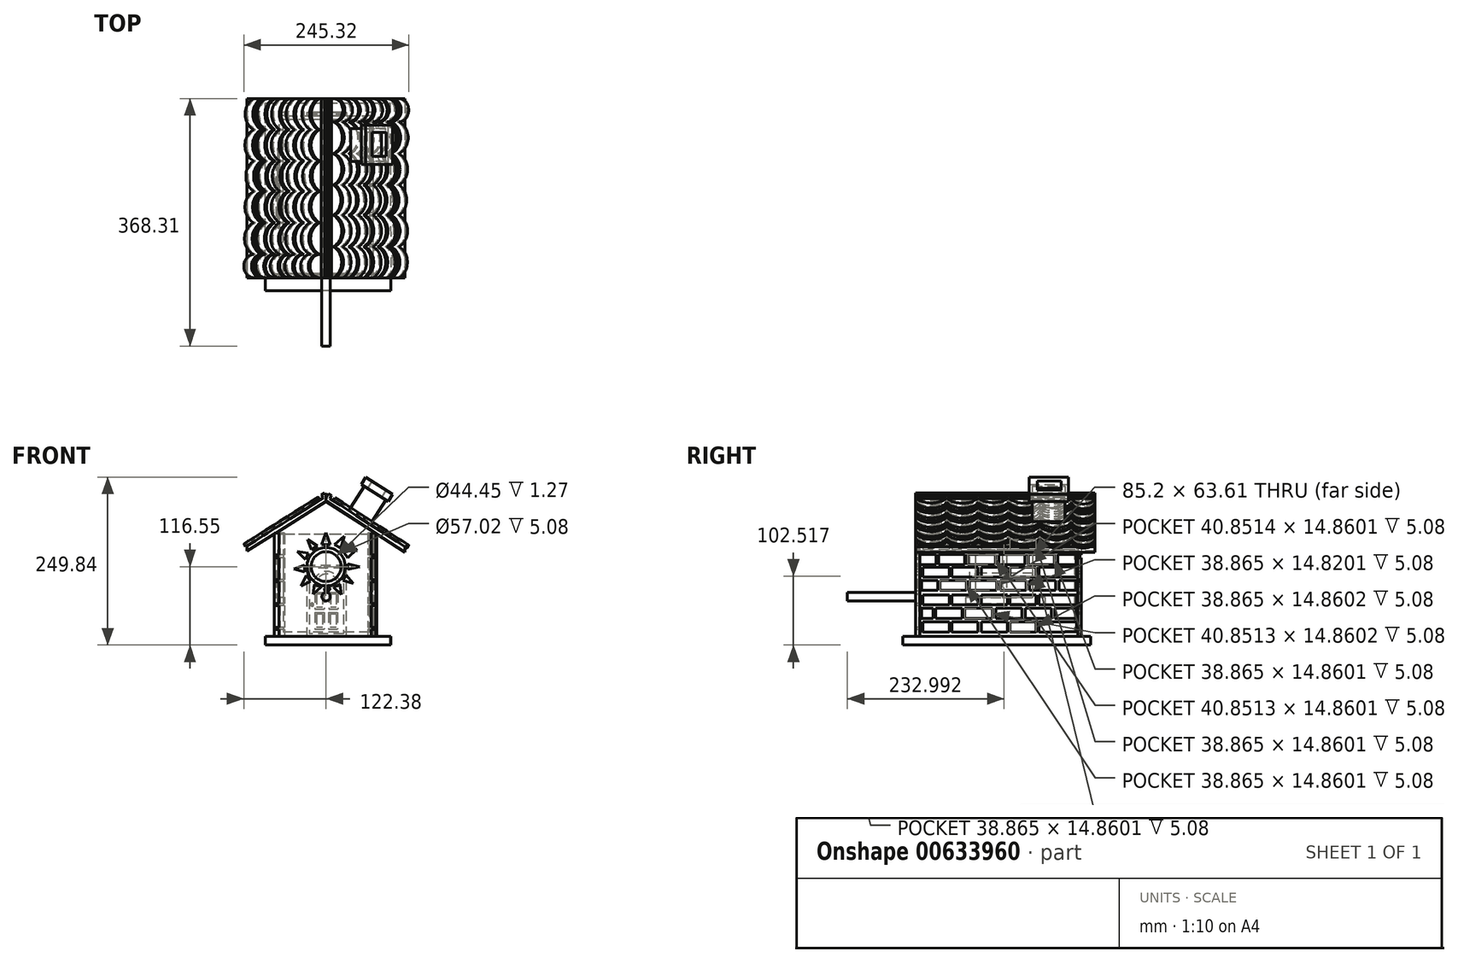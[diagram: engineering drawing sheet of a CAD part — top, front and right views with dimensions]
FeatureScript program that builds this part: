
annotation { "Feature Type Name" : "Feature", "Feature Type Description" : "" }
export const myFeature = defineFeature(function(context is Context, id is Id, definition is map)
    precondition{}
    {
        {
            var Q0;
            Q0=qCreatedBy(makeId("Front.planeOp"),FACE);
            var sketch = newSketch(context, id + "F0", { "sketchPlane" : qUnion([Q0])});
            skLineSegment(sketch, "E0", {"start": v(-77.05, 0) * mm, "end": v(75.35, 0) * mm});
            skLineSegment(sketch, "E1", {"start": v(75.35, 0) * mm, "end": v(75.35, 152.4) * mm});
            skLineSegment(sketch, "E2", {"start": v(-77.05, 0) * mm, "end": v(-77.05, 152.4) * mm});
            skLineSegment(sketch, "E3", {"start": v(-77.05, 152.4) * mm, "end": v(0, 200.95) * mm});
            skLineSegment(sketch, "E4", {"start": v(75.35, 152.4) * mm, "end": v(0, 200.95) * mm});
            skSolve(sketch);
        }
        {
            var Q0;
            Q0 = qSketchRegion(id + "F0", true);
            extrude(context, id + "F1", {"entities" : qUnion([Q0]), "oppositeDirection" : true, "depth" : 6.35 * mm, "offsetDistance" : 25.4 * mm});
        }
        {
            var Q0;
            Q0=qCreatedBy(makeId("Top.planeOp"),FACE);
            var sketch = newSketch(context, id + "F2", { "sketchPlane" : qUnion([Q0])});
            skLineSegment(sketch, "E5", {"start": v(69.98, 0) * mm, "end": v(69.98, 241.3) * mm});
            skLineSegment(sketch, "E6", {"start": v(-69.72, 0) * mm, "end": v(-69.72, 241.3) * mm});
            skLineSegment(sketch, "E7", {"start": v(-69.72, 241.3) * mm, "end": v(69.98, 241.3) * mm});
            skLineSegment(sketch, "E8", {"start": v(-72.26, 0) * mm, "end": v(67.44, 0) * mm});
            skLineSegment(sketch, "E9", {"start": v(-64.05, 5.89) * mm, "end": v(-64.05, 236.2) * mm});
            skLineSegment(sketch, "E10", {"start": v(-64.05, 236.2) * mm, "end": v(64.47, 236.2) * mm});
            skLineSegment(sketch, "E11", {"start": v(64.47, 236.2) * mm, "end": v(64.47, 5.89) * mm});
            skLineSegment(sketch, "E12", {"start": v(64.47, 5.89) * mm, "end": v(-64.05, 5.89) * mm});
            skLineSegment(sketch, "E13", {"start": v(-69.72, 0) * mm, "end": v(69.98, 0) * mm});
            skSolve(sketch);
        }
        {
            var Q0;
            Q0 = qSketchRegion(id + "F2", true);
            extrude(context, id + "F3", {"entities" : qUnion([Q0]), "operationType" : NewBodyOperationType.ADD, "depth" : 152.4 * mm, "offsetDistance" : 25.4 * mm});
        }
        {
            var Q0;
            Q0=qCreatedBy(makeId("Top.planeOp"),FACE);
            var sketch = newSketch(context, id + "F4", { "sketchPlane" : qUnion([Q0])});
            skLineSegment(sketch, "E14.0", {"start": v(-69.72, 0) * mm, "end": v(-69.72, 241.3) * mm});
            skLineSegment(sketch, "E15", {"start": v(69.65, 0) * mm, "end": v(69.65, 241.3) * mm});
            skLineSegment(sketch, "E16", {"start": v(-69.72, 241.3) * mm, "end": v(69.98, 241.3) * mm});
            skLineSegment(sketch, "E17", {"start": v(-69.72, 0) * mm, "end": v(69.98, 0) * mm});
            skSolve(sketch);
        }
        {
            var Q0;
            Q0 = qSketchRegion(id + "F4", true);
            extrude(context, id + "F5", {"entities" : qUnion([Q0]), "operationType" : NewBodyOperationType.ADD, "depth" : 6.35 * mm, "offsetDistance" : 25.4 * mm});
        }
        {
            var Q0;
            Q0=qCreatedBy(makeId("Front.planeOp"),FACE);
            var sketch = newSketch(context, id + "F6", { "sketchPlane" : qUnion([Q0])});
            skLineSegment(sketch, "E18.0", {"start": v(0, 200.95) * mm, "end": v(75.35, 152.4) * mm});
            skLineSegment(sketch, "E19.0", {"start": v(117.47, 125.54) * mm, "end": v(0.03, 201.21) * mm});
            skLineSegment(sketch, "E20", {"start": v(0.03, 201.21) * mm, "end": v(0.03, 208.85) * mm});
            skLineSegment(sketch, "E21", {"start": v(0.03, 208.85) * mm, "end": v(0.25, 208.7) * mm});
            skLineSegment(sketch, "E22.0", {"start": v(-77.05, 152.4) * mm, "end": v(0, 200.95) * mm});
            skLineSegment(sketch, "E23.0", {"start": v(-117.79, 126.84) * mm, "end": v(0.4, 201.32) * mm});
            skLineSegment(sketch, "E24.0", {"start": v(-117.93, 134.55) * mm, "end": v(0.26, 209.03) * mm});
            skLineSegment(sketch, "E25", {"start": v(-117.93, 134.55) * mm, "end": v(-117.79, 126.84) * mm});
            skLineSegment(sketch, "E26", {"start": v(0.03, 201.21) * mm, "end": v(0.26, 209.03) * mm});
            skLineSegment(sketch, "E27.0", {"start": v(117, 133.62) * mm, "end": v(-0.44, 209.3) * mm});
            skLineSegment(sketch, "E28", {"start": v(117.47, 125.54) * mm, "end": v(117, 133.62) * mm});
            skSolve(sketch);
        }
        {
            var Q0;
            Q0 = qSketchRegion(id + "F6", true);
            extrude(context, id + "F7", {"entities" : qUnion([Q0]), "oppositeDirection" : true, "depth" : 266.7 * mm, "offsetDistance" : 25.4 * mm});
        }
        {
            var Q0;
            Q0=qCreatedBy(makeId("Top.planeOp"),FACE);
            var sketch = newSketch(context, id + "F8", { "sketchPlane" : qUnion([Q0])});
            skLineSegment(sketch, "E29", {"start": v(96.42, -19.05) * mm, "end": v(-90.27, -19.05) * mm});
            skLineSegment(sketch, "E30", {"start": v(-90.27, -19.05) * mm, "end": v(-90.27, 260.35) * mm});
            skLineSegment(sketch, "E31", {"start": v(-90.27, 260.35) * mm, "end": v(95.05, 260.35) * mm});
            skLineSegment(sketch, "E32", {"start": v(95.05, 260.35) * mm, "end": v(96.42, -19.05) * mm});
            skSolve(sketch);
        }
        {
            var Q0;
            Q0 = qSketchRegion(id + "F8", true);
            extrude(context, id + "F9", {"entities" : qUnion([Q0]), "operationType" : NewBodyOperationType.ADD, "oppositeDirection" : true, "depth" : 12.7 * mm, "offsetDistance" : 25.4 * mm});
        }
        {
            var Q0;
            Q0=qCreatedBy(makeId("Front.planeOp"),FACE);
            var sketch = newSketch(context, id + "F10", { "sketchPlane" : qUnion([Q0])});
            skCircle(sketch, "E33", {"center": v(0, 103.85) * mm, "radius": 22.23 * mm});
            skSolve(sketch);
        }
        {
            var Q0;
            Q0 = qSketchRegion(id + "F10", true);
            extrude(context, id + "F11", {"entities" : qUnion([Q0]), "operationType" : NewBodyOperationType.REMOVE, "oppositeDirection" : true, "depth" : 25.4 * mm, "offsetDistance" : 25.4 * mm});
        }
        {
            var Q0;
            Q0=qCreatedBy(makeId("Front.planeOp"),FACE);
            var sketch = newSketch(context, id + "F12", { "sketchPlane" : qUnion([Q0])});
            skCircle(sketch, "E34", {"center": v(0, 59.27) * mm, "radius": 6.35 * mm});
            skSolve(sketch);
        }
        {
            var Q0;
            Q0 = qSketchRegion(id + "F12", true);
            extrude(context, id + "F13", {"entities" : qUnion([Q0]), "operationType" : NewBodyOperationType.ADD, "depth" : 101.6 * mm, "offsetDistance" : 25.4 * mm});
        }
        {
            var Q0;
            Q0=makeQuery(id+"F3.opExtrude","SWEPT_FACE",FACE,{"disambiguationData":[OSD([sQuery(id+"F2.wireOp",EDGE,"E6")])]});
            var sketch = newSketch(context, id + "F14", { "sketchPlane" : qUnion([Q0])});
            skLineSegment(sketch, "E35.bottom", {"start": v(-88.8, 121.62) * mm, "end": v(-174, 121.62) * mm});
            skLineSegment(sketch, "E35.top", {"start": v(-88.8, 58.01) * mm, "end": v(-174, 58.01) * mm});
            skLineSegment(sketch, "E35.left", {"start": v(-88.8, 121.62) * mm, "end": v(-88.8, 58.01) * mm});
            skLineSegment(sketch, "E35.right", {"start": v(-174, 121.62) * mm, "end": v(-174, 58.01) * mm});
            skPoint(sketch, "E35.middle", {"position": v(-131.4, 80.67) * mm});
            skSolve(sketch);
        }
        {
            var Q0;
            Q0 = qSketchRegion(id + "F14", true);
            extrude(context, id + "F15", {"entities" : qUnion([Q0]), "operationType" : NewBodyOperationType.REMOVE, "oppositeDirection" : true, "depth" : 25.4 * mm, "offsetDistance" : 25.4 * mm});
        }
        {
            var Q0;
            Q0=makeQuery(id+"F3.opExtrude","SWEPT_FACE",FACE,{"disambiguationData":[OSD([sQuery(id+"F2.wireOp",EDGE,"E6")])]});
            var sketch = newSketch(context, id + "F16", { "sketchPlane" : qUnion([Q0])});
            skLineSegment(sketch, "E36", {"start": v(-128.22, 58.01) * mm, "end": v(-131.4, 58.01) * mm});
            skLineSegment(sketch, "E37", {"start": v(-88.8, 89.82) * mm, "end": v(-88.8, 93) * mm});
            skLineSegment(sketch, "E38", {"start": v(-193.14, 58.01) * mm, "end": v(-74.26, 58.01) * mm});
            skLineSegment(sketch, "E39", {"start": v(-74.26, 58.01) * mm, "end": v(-74.26, 48.98) * mm});
            skLineSegment(sketch, "E40", {"start": v(-74.26, 48.98) * mm, "end": v(-193.14, 48.98) * mm});
            skLineSegment(sketch, "E41", {"start": v(-193.14, 48.98) * mm, "end": v(-193.14, 58.01) * mm});
            skLineSegment(sketch, "E42", {"start": v(-80.55, 58.01) * mm, "end": v(-80.55, 129) * mm});
            skLineSegment(sketch, "E43", {"start": v(-80.55, 129) * mm, "end": v(-181.71, 129) * mm});
            skLineSegment(sketch, "E44", {"start": v(-181.71, 129) * mm, "end": v(-181.71, 58.01) * mm});
            skLineSegment(sketch, "E45", {"start": v(-181.71, 58.01) * mm, "end": v(-174, 58.01) * mm});
            skLineSegment(sketch, "E46", {"start": v(-174, 58.01) * mm, "end": v(-174, 121.62) * mm});
            skLineSegment(sketch, "E47", {"start": v(-174, 121.62) * mm, "end": v(-88.8, 121.62) * mm});
            skLineSegment(sketch, "E48", {"start": v(-88.8, 121.62) * mm, "end": v(-88.8, 58.01) * mm});
            skLineSegment(sketch, "E49", {"start": v(-88.8, 58.01) * mm, "end": v(-80.55, 58.01) * mm});
            skLineSegment(sketch, "E50", {"start": v(-174, 93) * mm, "end": v(-174, 89.82) * mm});
            skLineSegment(sketch, "E51", {"start": v(-88.8, 93) * mm, "end": v(-88.8, 89.82) * mm});
            skLineSegment(sketch, "E52", {"start": v(-131.4, 121.62) * mm, "end": v(-128.22, 121.62) * mm});
            skSolve(sketch);
        }
        {
            var Q0;
            Q0 = qSketchRegion(id + "F16", true);
            extrude(context, id + "F17", {"entities" : qUnion([Q0]), "depth" : 2.54 * mm, "offsetDistance" : 25.4 * mm});
        }
        {
            var Q0;
            Q0=makeQuery(id+"F3.opExtrude","SWEPT_FACE",FACE,{"disambiguationData":[OSD([sQuery(id+"F2.wireOp",EDGE,"E6")])]});
            var sketch = newSketch(context, id + "F18", { "sketchPlane" : qUnion([Q0])});
            skLineSegment(sketch, "E53.bottom", {"start": v(-135.25, 121.62) * mm, "end": v(-128.63, 121.62) * mm});
            skLineSegment(sketch, "E53.top", {"start": v(-135.25, 58.01) * mm, "end": v(-128.63, 58.01) * mm});
            skLineSegment(sketch, "E53.left", {"start": v(-135.25, 121.62) * mm, "end": v(-135.25, 58.01) * mm});
            skLineSegment(sketch, "E53.right", {"start": v(-128.63, 121.62) * mm, "end": v(-128.63, 58.01) * mm});
            skLineSegment(sketch, "E54.bottom", {"start": v(-174, 94.33) * mm, "end": v(-88.8, 94.33) * mm});
            skLineSegment(sketch, "E54.top", {"start": v(-174, 87.38) * mm, "end": v(-88.8, 87.38) * mm});
            skLineSegment(sketch, "E54.left", {"start": v(-174, 94.33) * mm, "end": v(-174, 87.38) * mm});
            skLineSegment(sketch, "E54.right", {"start": v(-88.8, 94.33) * mm, "end": v(-88.8, 87.38) * mm});
            skSolve(sketch);
        }
        {
            var Q0;
            Q0 = qSketchRegion(id + "F18", true);
            extrude(context, id + "F19", {"entities" : qUnion([Q0]), "operationType" : NewBodyOperationType.ADD, "depth" : 5.08 * mm, "offsetDistance" : 25.4 * mm});
        }
        {
            var Q0;
            Q0=makeQuery(id+"F3.opExtrude","SWEPT_FACE",FACE,{"disambiguationData":[OSD([sQuery(id+"F2.wireOp",EDGE,"E5")])]});
            var sketch = newSketch(context, id + "F20", { "sketchPlane" : qUnion([Q0])});
            skLineSegment(sketch, "E55.bottom", {"start": v(53.69, 21.55) * mm, "end": v(92.55, 21.55) * mm});
            skLineSegment(sketch, "E55.top", {"start": v(53.69, 6.69) * mm, "end": v(92.55, 6.69) * mm});
            skLineSegment(sketch, "E55.left", {"start": v(53.69, 21.55) * mm, "end": v(53.69, 6.69) * mm});
            skLineSegment(sketch, "E55.right", {"start": v(92.55, 21.55) * mm, "end": v(92.55, 6.69) * mm});
            skLineSegment(sketch, "E56.bottom", {"start": v(97.41, 21.55) * mm, "end": v(136.28, 21.55) * mm});
            skLineSegment(sketch, "E56.top", {"start": v(97.41, 6.69) * mm, "end": v(136.28, 6.69) * mm});
            skLineSegment(sketch, "E56.left", {"start": v(97.41, 21.55) * mm, "end": v(97.41, 6.69) * mm});
            skLineSegment(sketch, "E56.right", {"start": v(136.28, 21.55) * mm, "end": v(136.28, 6.69) * mm});
            skLineSegment(sketch, "E57.bottom", {"start": v(140.34, 21.55) * mm, "end": v(179.2, 21.55) * mm});
            skLineSegment(sketch, "E57.top", {"start": v(140.34, 6.69) * mm, "end": v(179.2, 6.69) * mm});
            skLineSegment(sketch, "E57.left", {"start": v(140.34, 21.55) * mm, "end": v(140.34, 6.69) * mm});
            skLineSegment(sketch, "E57.right", {"start": v(179.2, 21.55) * mm, "end": v(179.2, 6.69) * mm});
            skLineSegment(sketch, "E58.bottom", {"start": v(183.42, 21.55) * mm, "end": v(222.29, 21.55) * mm});
            skLineSegment(sketch, "E58.top", {"start": v(183.42, 6.69) * mm, "end": v(222.29, 6.69) * mm});
            skLineSegment(sketch, "E58.left", {"start": v(183.42, 21.55) * mm, "end": v(183.42, 6.69) * mm});
            skLineSegment(sketch, "E58.right", {"start": v(222.29, 21.55) * mm, "end": v(222.29, 6.69) * mm});
            skLineSegment(sketch, "E59.bottom", {"start": v(10.92, 21.55) * mm, "end": v(49.79, 21.55) * mm});
            skLineSegment(sketch, "E59.top", {"start": v(10.92, 6.69) * mm, "end": v(49.79, 6.69) * mm});
            skLineSegment(sketch, "E59.left", {"start": v(10.92, 21.55) * mm, "end": v(10.92, 6.69) * mm});
            skLineSegment(sketch, "E59.right", {"start": v(49.79, 21.55) * mm, "end": v(49.79, 6.69) * mm});
            skLineSegment(sketch, "E60.bottom", {"start": v(119.36, 41.72) * mm, "end": v(158.22, 41.72) * mm});
            skLineSegment(sketch, "E60.top", {"start": v(119.36, 26.9) * mm, "end": v(158.22, 26.9) * mm});
            skLineSegment(sketch, "E60.left", {"start": v(119.36, 42.76) * mm, "end": v(119.36, 26.9) * mm});
            skLineSegment(sketch, "E60.right", {"start": v(158.22, 42.76) * mm, "end": v(158.22, 26.9) * mm});
            skLineSegment(sketch, "E61.bottom", {"start": v(73.2, 41.72) * mm, "end": v(114.05, 41.72) * mm});
            skLineSegment(sketch, "E61.top", {"start": v(73.2, 26.86) * mm, "end": v(114.05, 26.86) * mm});
            skLineSegment(sketch, "E61.left", {"start": v(73.2, 41.72) * mm, "end": v(73.2, 26.86) * mm});
            skLineSegment(sketch, "E61.right", {"start": v(114.05, 41.72) * mm, "end": v(114.05, 26.86) * mm});
            skLineSegment(sketch, "E62.bottom", {"start": v(163.05, 41.76) * mm, "end": v(201.91, 41.76) * mm});
            skLineSegment(sketch, "E62.top", {"start": v(163.05, 26.9) * mm, "end": v(201.91, 26.9) * mm});
            skLineSegment(sketch, "E62.left", {"start": v(163.05, 41.76) * mm, "end": v(163.05, 26.9) * mm});
            skLineSegment(sketch, "E62.right", {"start": v(201.91, 41.76) * mm, "end": v(201.91, 26.9) * mm});
            skLineSegment(sketch, "E63.bottom", {"start": v(29.94, 41.76) * mm, "end": v(68.8, 41.76) * mm});
            skLineSegment(sketch, "E63.top", {"start": v(29.94, 26.9) * mm, "end": v(68.8, 26.9) * mm});
            skLineSegment(sketch, "E63.left", {"start": v(29.94, 41.76) * mm, "end": v(29.94, 26.9) * mm});
            skLineSegment(sketch, "E63.right", {"start": v(68.8, 41.76) * mm, "end": v(68.8, 26.9) * mm});
            skLineSegment(sketch, "E64.bottom", {"start": v(206.96, 41.76) * mm, "end": v(238.93, 41.76) * mm});
            skLineSegment(sketch, "E64.top", {"start": v(206.96, 26.9) * mm, "end": v(238.93, 26.9) * mm});
            skLineSegment(sketch, "E64.left", {"start": v(206.96, 41.76) * mm, "end": v(206.96, 26.9) * mm});
            skLineSegment(sketch, "E64.right", {"start": v(238.93, 41.76) * mm, "end": v(238.93, 26.9) * mm});
            skLineSegment(sketch, "E65.bottom", {"start": v(8.48, 41.76) * mm, "end": v(26.16, 41.76) * mm});
            skLineSegment(sketch, "E65.top", {"start": v(8.48, 26.9) * mm, "end": v(26.16, 26.9) * mm});
            skLineSegment(sketch, "E65.left", {"start": v(8.48, 41.76) * mm, "end": v(8.48, 26.9) * mm});
            skLineSegment(sketch, "E65.right", {"start": v(26.16, 41.76) * mm, "end": v(26.16, 26.9) * mm});
            skLineSegment(sketch, "E66.bottom", {"start": v(218.23, 21.88) * mm, "end": v(239.36, 21.88) * mm});
            skLineSegment(sketch, "E66.top", {"start": v(218.23, 7.02) * mm, "end": v(239.36, 7.02) * mm});
            skLineSegment(sketch, "E66.left", {"start": v(218.23, 21.88) * mm, "end": v(218.23, 7.02) * mm});
            skLineSegment(sketch, "E66.right", {"start": v(239.36, 21.88) * mm, "end": v(239.36, 7.02) * mm});
            skLineSegment(sketch, "E67.bottom", {"start": v(53.69, 61.68) * mm, "end": v(92.55, 61.68) * mm});
            skLineSegment(sketch, "E67.top", {"start": v(53.69, 46.82) * mm, "end": v(92.55, 46.82) * mm});
            skLineSegment(sketch, "E67.left", {"start": v(53.69, 61.68) * mm, "end": v(53.69, 46.82) * mm});
            skLineSegment(sketch, "E67.right", {"start": v(92.55, 61.68) * mm, "end": v(92.55, 46.82) * mm});
            skLineSegment(sketch, "E68.bottom", {"start": v(97.41, 61.68) * mm, "end": v(136.28, 61.68) * mm});
            skLineSegment(sketch, "E68.top", {"start": v(97.41, 46.82) * mm, "end": v(136.28, 46.82) * mm});
            skLineSegment(sketch, "E68.left", {"start": v(97.41, 61.68) * mm, "end": v(97.41, 46.82) * mm});
            skLineSegment(sketch, "E68.right", {"start": v(136.28, 61.68) * mm, "end": v(136.28, 46.82) * mm});
            skLineSegment(sketch, "E69.bottom", {"start": v(140.34, 61.68) * mm, "end": v(179.2, 61.68) * mm});
            skLineSegment(sketch, "E69.top", {"start": v(140.34, 46.82) * mm, "end": v(179.2, 46.82) * mm});
            skLineSegment(sketch, "E69.left", {"start": v(140.34, 61.68) * mm, "end": v(140.34, 46.82) * mm});
            skLineSegment(sketch, "E69.right", {"start": v(179.2, 61.68) * mm, "end": v(179.2, 46.82) * mm});
            skLineSegment(sketch, "E70.bottom", {"start": v(183.42, 61.68) * mm, "end": v(222.29, 61.68) * mm});
            skLineSegment(sketch, "E70.top", {"start": v(183.42, 46.82) * mm, "end": v(222.29, 46.82) * mm});
            skLineSegment(sketch, "E70.left", {"start": v(183.42, 61.68) * mm, "end": v(183.42, 46.82) * mm});
            skLineSegment(sketch, "E70.right", {"start": v(222.29, 61.68) * mm, "end": v(222.29, 46.82) * mm});
            skLineSegment(sketch, "E71.bottom", {"start": v(10.92, 61.68) * mm, "end": v(49.79, 61.68) * mm});
            skLineSegment(sketch, "E71.top", {"start": v(10.92, 46.82) * mm, "end": v(49.79, 46.82) * mm});
            skLineSegment(sketch, "E71.left", {"start": v(10.92, 61.68) * mm, "end": v(10.92, 46.82) * mm});
            skLineSegment(sketch, "E71.right", {"start": v(49.79, 61.68) * mm, "end": v(49.79, 46.82) * mm});
            skLineSegment(sketch, "E72.bottom", {"start": v(218.23, 62.02) * mm, "end": v(239.36, 62.02) * mm});
            skLineSegment(sketch, "E72.top", {"start": v(218.23, 47.16) * mm, "end": v(239.36, 47.16) * mm});
            skLineSegment(sketch, "E72.left", {"start": v(218.23, 62.02) * mm, "end": v(218.23, 47.16) * mm});
            skLineSegment(sketch, "E72.right", {"start": v(239.36, 62.02) * mm, "end": v(239.36, 47.16) * mm});
            skLineSegment(sketch, "E73.bottom", {"start": v(125.77, 83.38) * mm, "end": v(164.64, 83.38) * mm});
            skLineSegment(sketch, "E73.top", {"start": v(125.77, 68.56) * mm, "end": v(164.64, 68.56) * mm});
            skLineSegment(sketch, "E73.left", {"start": v(125.77, 84.41) * mm, "end": v(125.77, 68.56) * mm});
            skLineSegment(sketch, "E73.right", {"start": v(164.64, 84.41) * mm, "end": v(164.64, 68.56) * mm});
            skLineSegment(sketch, "E74.bottom", {"start": v(79.61, 83.38) * mm, "end": v(120.46, 83.38) * mm});
            skLineSegment(sketch, "E74.top", {"start": v(79.61, 68.52) * mm, "end": v(120.46, 68.52) * mm});
            skLineSegment(sketch, "E74.left", {"start": v(79.61, 83.38) * mm, "end": v(79.61, 68.52) * mm});
            skLineSegment(sketch, "E74.right", {"start": v(120.46, 83.38) * mm, "end": v(120.46, 68.52) * mm});
            skLineSegment(sketch, "E75.bottom", {"start": v(169.46, 83.42) * mm, "end": v(208.33, 83.42) * mm});
            skLineSegment(sketch, "E75.top", {"start": v(169.46, 68.56) * mm, "end": v(208.33, 68.56) * mm});
            skLineSegment(sketch, "E75.left", {"start": v(169.46, 83.42) * mm, "end": v(169.46, 68.56) * mm});
            skLineSegment(sketch, "E75.right", {"start": v(208.33, 83.42) * mm, "end": v(208.33, 68.56) * mm});
            skLineSegment(sketch, "E76.bottom", {"start": v(36.36, 83.42) * mm, "end": v(75.22, 83.42) * mm});
            skLineSegment(sketch, "E76.top", {"start": v(36.36, 68.56) * mm, "end": v(75.22, 68.56) * mm});
            skLineSegment(sketch, "E76.left", {"start": v(36.36, 83.42) * mm, "end": v(36.36, 68.56) * mm});
            skLineSegment(sketch, "E76.right", {"start": v(75.22, 83.42) * mm, "end": v(75.22, 68.56) * mm});
            skLineSegment(sketch, "E77.bottom", {"start": v(213.38, 83.42) * mm, "end": v(238.94, 83.42) * mm});
            skLineSegment(sketch, "E77.top", {"start": v(213.38, 68.56) * mm, "end": v(238.94, 68.56) * mm});
            skLineSegment(sketch, "E77.left", {"start": v(213.38, 83.42) * mm, "end": v(213.38, 68.56) * mm});
            skLineSegment(sketch, "E77.right", {"start": v(238.94, 83.42) * mm, "end": v(238.94, 68.56) * mm});
            skLineSegment(sketch, "E78.bottom", {"start": v(8.49, 83.42) * mm, "end": v(32.58, 83.42) * mm});
            skLineSegment(sketch, "E78.top", {"start": v(8.49, 68.56) * mm, "end": v(32.58, 68.56) * mm});
            skLineSegment(sketch, "E78.left", {"start": v(8.49, 83.42) * mm, "end": v(8.49, 68.56) * mm});
            skLineSegment(sketch, "E78.right", {"start": v(32.58, 83.42) * mm, "end": v(32.58, 68.56) * mm});
            skLineSegment(sketch, "E79.bottom", {"start": v(53.69, 103.1) * mm, "end": v(92.55, 103.1) * mm});
            skLineSegment(sketch, "E79.top", {"start": v(53.69, 88.24) * mm, "end": v(92.55, 88.24) * mm});
            skLineSegment(sketch, "E79.left", {"start": v(53.69, 103.1) * mm, "end": v(53.69, 88.24) * mm});
            skLineSegment(sketch, "E79.right", {"start": v(92.55, 103.1) * mm, "end": v(92.55, 88.24) * mm});
            skLineSegment(sketch, "E80.bottom", {"start": v(97.41, 103.1) * mm, "end": v(136.28, 103.1) * mm});
            skLineSegment(sketch, "E80.top", {"start": v(97.41, 88.24) * mm, "end": v(136.28, 88.24) * mm});
            skLineSegment(sketch, "E80.left", {"start": v(97.41, 103.1) * mm, "end": v(97.41, 88.24) * mm});
            skLineSegment(sketch, "E80.right", {"start": v(136.28, 103.1) * mm, "end": v(136.28, 88.24) * mm});
            skLineSegment(sketch, "E81.bottom", {"start": v(140.34, 103.1) * mm, "end": v(179.2, 103.1) * mm});
            skLineSegment(sketch, "E81.top", {"start": v(140.34, 88.24) * mm, "end": v(179.2, 88.24) * mm});
            skLineSegment(sketch, "E81.left", {"start": v(140.34, 103.1) * mm, "end": v(140.34, 88.24) * mm});
            skLineSegment(sketch, "E81.right", {"start": v(179.2, 103.1) * mm, "end": v(179.2, 88.24) * mm});
            skLineSegment(sketch, "E82.bottom", {"start": v(183.42, 103.1) * mm, "end": v(222.29, 103.1) * mm});
            skLineSegment(sketch, "E82.top", {"start": v(183.42, 88.24) * mm, "end": v(222.29, 88.24) * mm});
            skLineSegment(sketch, "E82.left", {"start": v(183.42, 103.1) * mm, "end": v(183.42, 88.24) * mm});
            skLineSegment(sketch, "E82.right", {"start": v(222.29, 103.1) * mm, "end": v(222.29, 88.24) * mm});
            skLineSegment(sketch, "E83.bottom", {"start": v(10.92, 103.1) * mm, "end": v(49.79, 103.1) * mm});
            skLineSegment(sketch, "E83.top", {"start": v(10.92, 88.24) * mm, "end": v(49.79, 88.24) * mm});
            skLineSegment(sketch, "E83.left", {"start": v(10.92, 103.1) * mm, "end": v(10.92, 88.24) * mm});
            skLineSegment(sketch, "E83.right", {"start": v(49.79, 103.1) * mm, "end": v(49.79, 88.24) * mm});
            skLineSegment(sketch, "E84.bottom", {"start": v(218.23, 103.44) * mm, "end": v(239.36, 103.44) * mm});
            skLineSegment(sketch, "E84.top", {"start": v(218.23, 88.58) * mm, "end": v(239.36, 88.58) * mm});
            skLineSegment(sketch, "E84.left", {"start": v(218.23, 103.44) * mm, "end": v(218.23, 88.58) * mm});
            skLineSegment(sketch, "E84.right", {"start": v(239.36, 103.44) * mm, "end": v(239.36, 88.58) * mm});
            skLineSegment(sketch, "E85.bottom", {"start": v(123.63, 121.8) * mm, "end": v(162.5, 121.8) * mm});
            skLineSegment(sketch, "E85.top", {"start": v(123.63, 106.98) * mm, "end": v(162.5, 106.98) * mm});
            skLineSegment(sketch, "E85.left", {"start": v(123.63, 122.83) * mm, "end": v(123.63, 106.98) * mm});
            skLineSegment(sketch, "E85.right", {"start": v(162.5, 122.83) * mm, "end": v(162.5, 106.98) * mm});
            skLineSegment(sketch, "E86.bottom", {"start": v(77.47, 121.8) * mm, "end": v(118.32, 121.8) * mm});
            skLineSegment(sketch, "E86.top", {"start": v(77.47, 106.94) * mm, "end": v(118.32, 106.94) * mm});
            skLineSegment(sketch, "E86.left", {"start": v(77.47, 121.8) * mm, "end": v(77.47, 106.94) * mm});
            skLineSegment(sketch, "E86.right", {"start": v(118.32, 121.8) * mm, "end": v(118.32, 106.94) * mm});
            skLineSegment(sketch, "E87.bottom", {"start": v(167.32, 121.84) * mm, "end": v(206.19, 121.84) * mm});
            skLineSegment(sketch, "E87.top", {"start": v(167.32, 106.98) * mm, "end": v(206.19, 106.98) * mm});
            skLineSegment(sketch, "E87.left", {"start": v(167.32, 121.84) * mm, "end": v(167.32, 106.98) * mm});
            skLineSegment(sketch, "E87.right", {"start": v(206.19, 121.84) * mm, "end": v(206.19, 106.98) * mm});
            skLineSegment(sketch, "E88.bottom", {"start": v(34.22, 121.84) * mm, "end": v(73.08, 121.84) * mm});
            skLineSegment(sketch, "E88.top", {"start": v(34.22, 106.98) * mm, "end": v(73.08, 106.98) * mm});
            skLineSegment(sketch, "E88.left", {"start": v(34.22, 121.84) * mm, "end": v(34.22, 106.98) * mm});
            skLineSegment(sketch, "E88.right", {"start": v(73.08, 121.84) * mm, "end": v(73.08, 106.98) * mm});
            skLineSegment(sketch, "E89.bottom", {"start": v(211.24, 121.84) * mm, "end": v(238.77, 121.84) * mm});
            skLineSegment(sketch, "E89.top", {"start": v(211.24, 106.98) * mm, "end": v(238.77, 106.98) * mm});
            skLineSegment(sketch, "E89.left", {"start": v(211.24, 121.84) * mm, "end": v(211.24, 106.98) * mm});
            skLineSegment(sketch, "E89.right", {"start": v(238.77, 121.84) * mm, "end": v(238.77, 106.98) * mm});
            skLineSegment(sketch, "E90.bottom", {"start": v(6.35, 121.84) * mm, "end": v(30.44, 121.84) * mm});
            skLineSegment(sketch, "E90.top", {"start": v(6.35, 106.98) * mm, "end": v(30.44, 106.98) * mm});
            skLineSegment(sketch, "E90.left", {"start": v(6.35, 121.84) * mm, "end": v(6.35, 106.98) * mm});
            skLineSegment(sketch, "E90.right", {"start": v(30.44, 121.84) * mm, "end": v(30.44, 106.98) * mm});
            skLineSegment(sketch, "E91.bottom", {"start": v(53.69, 144.31) * mm, "end": v(92.55, 144.31) * mm});
            skLineSegment(sketch, "E91.top", {"start": v(53.69, 129.45) * mm, "end": v(92.55, 129.45) * mm});
            skLineSegment(sketch, "E91.left", {"start": v(53.69, 144.31) * mm, "end": v(53.69, 129.45) * mm});
            skLineSegment(sketch, "E91.right", {"start": v(92.55, 144.31) * mm, "end": v(92.55, 129.45) * mm});
            skLineSegment(sketch, "E92.bottom", {"start": v(97.41, 144.31) * mm, "end": v(136.28, 144.31) * mm});
            skLineSegment(sketch, "E92.top", {"start": v(97.41, 129.45) * mm, "end": v(136.28, 129.45) * mm});
            skLineSegment(sketch, "E92.left", {"start": v(97.41, 144.31) * mm, "end": v(97.41, 129.45) * mm});
            skLineSegment(sketch, "E92.right", {"start": v(136.28, 144.31) * mm, "end": v(136.28, 129.45) * mm});
            skLineSegment(sketch, "E93.bottom", {"start": v(140.34, 144.31) * mm, "end": v(179.2, 144.31) * mm});
            skLineSegment(sketch, "E93.top", {"start": v(140.34, 129.45) * mm, "end": v(179.2, 129.45) * mm});
            skLineSegment(sketch, "E93.left", {"start": v(140.34, 144.31) * mm, "end": v(140.34, 129.45) * mm});
            skLineSegment(sketch, "E93.right", {"start": v(179.2, 144.31) * mm, "end": v(179.2, 129.45) * mm});
            skLineSegment(sketch, "E94.bottom", {"start": v(183.42, 144.31) * mm, "end": v(222.29, 144.31) * mm});
            skLineSegment(sketch, "E94.top", {"start": v(183.42, 129.45) * mm, "end": v(222.29, 129.45) * mm});
            skLineSegment(sketch, "E94.left", {"start": v(183.42, 144.31) * mm, "end": v(183.42, 129.45) * mm});
            skLineSegment(sketch, "E94.right", {"start": v(222.29, 144.31) * mm, "end": v(222.29, 129.45) * mm});
            skLineSegment(sketch, "E95.bottom", {"start": v(10.92, 144.31) * mm, "end": v(49.79, 144.31) * mm});
            skLineSegment(sketch, "E95.top", {"start": v(10.92, 129.45) * mm, "end": v(49.79, 129.45) * mm});
            skLineSegment(sketch, "E95.left", {"start": v(10.92, 144.31) * mm, "end": v(10.92, 129.45) * mm});
            skLineSegment(sketch, "E95.right", {"start": v(49.79, 144.31) * mm, "end": v(49.79, 129.45) * mm});
            skLineSegment(sketch, "E96.bottom", {"start": v(218.23, 144.65) * mm, "end": v(239.36, 144.65) * mm});
            skLineSegment(sketch, "E96.top", {"start": v(218.23, 129.79) * mm, "end": v(239.36, 129.79) * mm});
            skLineSegment(sketch, "E96.left", {"start": v(218.23, 144.65) * mm, "end": v(218.23, 129.79) * mm});
            skLineSegment(sketch, "E96.right", {"start": v(239.36, 144.65) * mm, "end": v(239.36, 129.79) * mm});
            skSolve(sketch);
        }
        {
            var Q0;
            Q0 = qSketchRegion(id + "F20", true);
            extrude(context, id + "F21", {"entities" : qUnion([Q0]), "operationType" : NewBodyOperationType.REMOVE, "oppositeDirection" : true, "depth" : 5.08 * mm, "offsetDistance" : 25.4 * mm});
        }
        {
            var Q0;
            Q0=makeQuery(id+"F1.opExtrude","CAP_FACE",FACE,{"disambiguationData":[OSD([sQuery(id+"F0.wireOp",EDGE,"E0"),sQuery(id+"F0.wireOp",EDGE,"E1"),sQuery(id+"F0.wireOp",EDGE,"E2"),sQuery(id+"F0.wireOp",EDGE,"E3"),sQuery(id+"F0.wireOp",EDGE,"E4")])],"isStart":true});
            var sketch = newSketch(context, id + "F22", { "sketchPlane" : qUnion([Q0])});
            skLineSegment(sketch, "E97.bottom", {"start": v(-77.05, 153.96) * mm, "end": v(-69.86, 153.96) * mm});
            skLineSegment(sketch, "E97.top", {"start": v(-77.05, 121.57) * mm, "end": v(-69.86, 121.57) * mm});
            skLineSegment(sketch, "E97.left", {"start": v(-77.05, 153.96) * mm, "end": v(-77.05, 121.57) * mm});
            skLineSegment(sketch, "E97.right", {"start": v(-69.86, 153.96) * mm, "end": v(-69.86, 121.57) * mm});
            skLineSegment(sketch, "E98.bottom", {"start": v(-77.05, 117.13) * mm, "end": v(-69.86, 117.13) * mm});
            skLineSegment(sketch, "E98.top", {"start": v(-77.05, 84.73) * mm, "end": v(-69.86, 84.73) * mm});
            skLineSegment(sketch, "E98.left", {"start": v(-77.05, 117.13) * mm, "end": v(-77.05, 84.73) * mm});
            skLineSegment(sketch, "E98.right", {"start": v(-69.86, 117.13) * mm, "end": v(-69.86, 84.73) * mm});
            skLineSegment(sketch, "E99.bottom", {"start": v(-77.05, 81.47) * mm, "end": v(-69.86, 81.47) * mm});
            skLineSegment(sketch, "E99.top", {"start": v(-77.05, 49.08) * mm, "end": v(-69.86, 49.08) * mm});
            skLineSegment(sketch, "E99.left", {"start": v(-77.05, 81.47) * mm, "end": v(-77.05, 49.08) * mm});
            skLineSegment(sketch, "E99.right", {"start": v(-69.86, 81.47) * mm, "end": v(-69.86, 49.08) * mm});
            skLineSegment(sketch, "E100.bottom", {"start": v(-77.05, 46.15) * mm, "end": v(-69.86, 46.15) * mm});
            skLineSegment(sketch, "E100.top", {"start": v(-77.05, 13.75) * mm, "end": v(-69.86, 13.75) * mm});
            skLineSegment(sketch, "E100.left", {"start": v(-77.05, 46.15) * mm, "end": v(-77.05, 13.75) * mm});
            skLineSegment(sketch, "E100.right", {"start": v(-69.86, 46.15) * mm, "end": v(-69.86, 13.75) * mm});
            skLineSegment(sketch, "E101.bottom", {"start": v(-77.05, 10.22) * mm, "end": v(-69.86, 10.22) * mm});
            skLineSegment(sketch, "E101.top", {"start": v(-77.05, 0.1) * mm, "end": v(-69.86, 0.1) * mm});
            skLineSegment(sketch, "E101.left", {"start": v(-77.05, 10.22) * mm, "end": v(-77.05, 0.1) * mm});
            skLineSegment(sketch, "E101.right", {"start": v(-69.86, 10.22) * mm, "end": v(-69.86, 0.1) * mm});
            skLineSegment(sketch, "E102.bottom", {"start": v(67.12, 153.86) * mm, "end": v(74.3, 153.86) * mm});
            skLineSegment(sketch, "E102.top", {"start": v(67.12, 121.47) * mm, "end": v(74.3, 121.47) * mm});
            skLineSegment(sketch, "E102.left", {"start": v(67.12, 153.86) * mm, "end": v(67.12, 121.47) * mm});
            skLineSegment(sketch, "E102.right", {"start": v(74.3, 153.86) * mm, "end": v(74.3, 121.47) * mm});
            skLineSegment(sketch, "E103.bottom", {"start": v(67.12, 117.03) * mm, "end": v(74.3, 117.03) * mm});
            skLineSegment(sketch, "E103.top", {"start": v(67.12, 84.63) * mm, "end": v(74.3, 84.63) * mm});
            skLineSegment(sketch, "E103.left", {"start": v(67.12, 117.03) * mm, "end": v(67.12, 84.63) * mm});
            skLineSegment(sketch, "E103.right", {"start": v(74.3, 117.03) * mm, "end": v(74.3, 84.63) * mm});
            skLineSegment(sketch, "E104.bottom", {"start": v(67.12, 81.37) * mm, "end": v(74.3, 81.37) * mm});
            skLineSegment(sketch, "E104.top", {"start": v(67.12, 48.98) * mm, "end": v(74.3, 48.98) * mm});
            skLineSegment(sketch, "E104.left", {"start": v(67.12, 81.37) * mm, "end": v(67.12, 48.98) * mm});
            skLineSegment(sketch, "E104.right", {"start": v(74.3, 81.37) * mm, "end": v(74.3, 48.98) * mm});
            skLineSegment(sketch, "E105.bottom", {"start": v(67.12, 46.05) * mm, "end": v(74.3, 46.05) * mm});
            skLineSegment(sketch, "E105.top", {"start": v(67.12, 13.65) * mm, "end": v(74.3, 13.65) * mm});
            skLineSegment(sketch, "E105.left", {"start": v(67.12, 46.05) * mm, "end": v(67.12, 13.65) * mm});
            skLineSegment(sketch, "E105.right", {"start": v(74.3, 46.05) * mm, "end": v(74.3, 13.65) * mm});
            skLineSegment(sketch, "E106.bottom", {"start": v(67.12, 10.12) * mm, "end": v(74.3, 10.12) * mm});
            skLineSegment(sketch, "E106.top", {"start": v(67.12, 0) * mm, "end": v(74.3, 0) * mm});
            skLineSegment(sketch, "E106.left", {"start": v(67.12, 10.12) * mm, "end": v(67.12, 0) * mm});
            skLineSegment(sketch, "E106.right", {"start": v(74.3, 10.12) * mm, "end": v(74.3, 0) * mm});
            skCircle(sketch, "E107", {"center": v(0, 103.85) * mm, "radius": 28.51 * mm});
            skLineSegment(sketch, "E108", {"start": v(-6.32, 136.64) * mm, "end": v(5.8, 136.64) * mm});
            skLineSegment(sketch, "E109", {"start": v(5.8, 136.64) * mm, "end": v(0, 154.25) * mm});
            skLineSegment(sketch, "E110", {"start": v(0, 154.25) * mm, "end": v(-6.32, 136.64) * mm});
            skLineSegment(sketch, "E111", {"start": v(12.4, 136.64) * mm, "end": v(21.93, 131.5) * mm});
            skLineSegment(sketch, "E112", {"start": v(21.93, 131.5) * mm, "end": v(27.07, 149.11) * mm});
            skLineSegment(sketch, "E113", {"start": v(27.07, 149.11) * mm, "end": v(12.4, 136.64) * mm});
            skLineSegment(sketch, "E114", {"start": v(26.34, 125.26) * mm, "end": v(31.84, 117.19) * mm});
            skLineSegment(sketch, "E115", {"start": v(31.84, 117.19) * mm, "end": v(45.78, 130.4) * mm});
            skLineSegment(sketch, "E116", {"start": v(45.78, 130.4) * mm, "end": v(26.34, 125.26) * mm});
            skLineSegment(sketch, "E117", {"start": v(32.2, 108.02) * mm, "end": v(32.2, 99.58) * mm});
            skLineSegment(sketch, "E118", {"start": v(32.2, 99.58) * mm, "end": v(50.19, 103.61) * mm});
            skLineSegment(sketch, "E119", {"start": v(50.19, 103.61) * mm, "end": v(32.2, 108.02) * mm});
            skLineSegment(sketch, "E120", {"start": v(29.64, 91.87) * mm, "end": v(24.87, 83.43) * mm});
            skLineSegment(sketch, "E121", {"start": v(24.87, 83.43) * mm, "end": v(40.28, 79.03) * mm});
            skLineSegment(sketch, "E122", {"start": v(40.28, 79.03) * mm, "end": v(29.64, 91.87) * mm});
            skLineSegment(sketch, "E123", {"start": v(20.47, 77.56) * mm, "end": v(11.03, 73.24) * mm});
            skLineSegment(sketch, "E124", {"start": v(11.03, 73.24) * mm, "end": v(22.83, 62.62) * mm});
            skLineSegment(sketch, "E125", {"start": v(22.83, 62.62) * mm, "end": v(20.47, 77.56) * mm});
            skLineSegment(sketch, "E126", {"start": v(-22.1, 129.3) * mm, "end": v(-12.92, 134.8) * mm});
            skLineSegment(sketch, "E127", {"start": v(-12.92, 134.8) * mm, "end": v(-27.6, 144.34) * mm});
            skLineSegment(sketch, "E128", {"start": v(-27.6, 144.34) * mm, "end": v(-22.1, 129.3) * mm});
            skLineSegment(sketch, "E129", {"start": v(-26.13, 123.8) * mm, "end": v(-30.9, 114.62) * mm});
            skLineSegment(sketch, "E130", {"start": v(-30.9, 114.62) * mm, "end": v(-43.01, 126.73) * mm});
            skLineSegment(sketch, "E131", {"start": v(-43.01, 126.73) * mm, "end": v(-26.13, 123.8) * mm});
            skLineSegment(sketch, "E132", {"start": v(-32.1, 105.89) * mm, "end": v(-32.1, 96.1) * mm});
            skLineSegment(sketch, "E133", {"start": v(-32.1, 96.1) * mm, "end": v(-47.6, 100.45) * mm});
            skLineSegment(sketch, "E134", {"start": v(-47.6, 100.45) * mm, "end": v(-32.1, 105.89) * mm});
            skLineSegment(sketch, "E135", {"start": v(-29.65, 90.92) * mm, "end": v(-22.85, 81.94) * mm});
            skLineSegment(sketch, "E136", {"start": v(-22.85, 81.94) * mm, "end": v(-37.27, 74.87) * mm});
            skLineSegment(sketch, "E137", {"start": v(-37.27, 74.87) * mm, "end": v(-29.65, 90.92) * mm});
            skLineSegment(sketch, "E138", {"start": v(-17.67, 77.86) * mm, "end": v(-7.33, 73.5) * mm});
            skLineSegment(sketch, "E139", {"start": v(-7.33, 73.5) * mm, "end": v(-19.04, 63.17) * mm});
            skLineSegment(sketch, "E140", {"start": v(-19.04, 63.17) * mm, "end": v(-17.67, 77.86) * mm});
            skLineSegment(sketch, "E141", {"start": v(-2.98, 72.14) * mm, "end": v(6.69, 72.14) * mm});
            skLineSegment(sketch, "E142", {"start": v(-2.98, 72.14) * mm, "end": v(-1.65, 67.7) * mm});
            skLineSegment(sketch, "E143", {"start": v(-1.65, 67.7) * mm, "end": v(3.61, 67.7) * mm});
            skLineSegment(sketch, "E144", {"start": v(3.61, 67.7) * mm, "end": v(6.69, 72.14) * mm});
            skSolve(sketch);
        }
        {
            var Q0;
            Q0 = qSketchRegion(id + "F22", true);
            extrude(context, id + "F23", {"entities" : qUnion([Q0]), "operationType" : NewBodyOperationType.REMOVE, "oppositeDirection" : true, "depth" : 5.08 * mm, "offsetDistance" : 25.4 * mm});
        }
        {
            var Q0;
            Q0=makeQuery(id+"F7.opExtrude","SWEPT_FACE",FACE,{"disambiguationData":[OSD([sQuery(id+"F6.wireOp",EDGE,"E24.0")])]});
            var sketch = newSketch(context, id + "F24", { "sketchPlane" : qUnion([Q0])});
            skLineSegment(sketch, "E145.bottom", {"start": v(111.66, 266.7) * mm, "end": v(106.34, 266.7) * mm});
            skLineSegment(sketch, "E145.top", {"start": v(111.66, 0) * mm, "end": v(106.34, 0) * mm});
            skLineSegment(sketch, "E145.left", {"start": v(111.66, 266.7) * mm, "end": v(111.66, 0) * mm});
            skLineSegment(sketch, "E146", {"start": v(106.34, 266.7) * mm, "end": v(106.34, 0) * mm});
            skLineSegment(sketch, "E147.bottom", {"start": v(105.77, 266.7) * mm, "end": v(100.45, 266.7) * mm});
            skLineSegment(sketch, "E147.top", {"start": v(105.77, 0) * mm, "end": v(100.45, 0) * mm});
            skArc(sketch, "E148", {"start": v(100.45, 266.7) * mm, "mid": v(85.55, 243.57) * mm, "end": v(100.45, 220.44) * mm});
            skArc(sketch, "E149", {"start": v(100.45, 220.44) * mm, "mid": v(85.06, 197.1) * mm, "end": v(100.45, 173.76) * mm});
            skArc(sketch, "E150", {"start": v(100.45, 173.76) * mm, "mid": v(86.75, 151.22) * mm, "end": v(100.45, 128.67) * mm});
            skArc(sketch, "E151", {"start": v(100.45, 128.67) * mm, "mid": v(85.04, 105.32) * mm, "end": v(100.45, 81.97) * mm});
            skArc(sketch, "E152", {"start": v(100.45, 81.97) * mm, "mid": v(84.2, 58.28) * mm, "end": v(100.45, 34.59) * mm});
            skArc(sketch, "E153", {"start": v(100.45, 34.59) * mm, "mid": v(83.15, 17.3) * mm, "end": v(100.45, 0) * mm});
            skLineSegment(sketch, "E154.bottom", {"start": v(92.22, 266.71) * mm, "end": v(86.9, 266.71) * mm});
            skLineSegment(sketch, "E154.top", {"start": v(92.22, 0.01) * mm, "end": v(86.9, 0.01) * mm});
            skArc(sketch, "E155", {"start": v(86.9, 266.71) * mm, "mid": v(72, 243.58) * mm, "end": v(86.9, 220.45) * mm});
            skArc(sketch, "E156", {"start": v(86.9, 220.45) * mm, "mid": v(71.52, 197.11) * mm, "end": v(86.9, 173.77) * mm});
            skArc(sketch, "E157", {"start": v(86.9, 173.77) * mm, "mid": v(73.2, 151.23) * mm, "end": v(86.9, 128.68) * mm});
            skArc(sketch, "E158", {"start": v(86.9, 128.68) * mm, "mid": v(71.5, 105.33) * mm, "end": v(86.9, 81.98) * mm});
            skArc(sketch, "E159", {"start": v(86.9, 81.98) * mm, "mid": v(70.66, 58.29) * mm, "end": v(86.9, 34.6) * mm});
            skArc(sketch, "E160", {"start": v(86.9, 34.6) * mm, "mid": v(69.61, 17.3) * mm, "end": v(86.9, 0.01) * mm});
            skLineSegment(sketch, "E161", {"start": v(86.9, 266.71) * mm, "end": v(100.45, 266.7) * mm});
            skLineSegment(sketch, "E162", {"start": v(86.9, 0.01) * mm, "end": v(100.45, 0) * mm});
            skLineSegment(sketch, "E163.bottom", {"start": v(78.19, 266.69) * mm, "end": v(72.87, 266.69) * mm});
            skLineSegment(sketch, "E163.top", {"start": v(78.19, -0.01) * mm, "end": v(72.87, -0.01) * mm});
            skArc(sketch, "E164", {"start": v(72.87, 266.69) * mm, "mid": v(57.97, 243.56) * mm, "end": v(72.87, 220.43) * mm});
            skArc(sketch, "E165", {"start": v(72.87, 220.43) * mm, "mid": v(57.49, 197.1) * mm, "end": v(72.87, 173.75) * mm});
            skArc(sketch, "E166", {"start": v(72.87, 173.75) * mm, "mid": v(59.17, 151.2) * mm, "end": v(72.87, 128.66) * mm});
            skArc(sketch, "E167", {"start": v(72.87, 128.66) * mm, "mid": v(57.46, 105.3) * mm, "end": v(72.87, 81.96) * mm});
            skArc(sketch, "E168", {"start": v(72.87, 81.96) * mm, "mid": v(56.63, 58.27) * mm, "end": v(72.87, 34.58) * mm});
            skArc(sketch, "E169", {"start": v(72.87, 34.58) * mm, "mid": v(55.58, 17.28) * mm, "end": v(72.87, -0.01) * mm});
            skLineSegment(sketch, "E170.bottom", {"start": v(64.64, 266.7) * mm, "end": v(59.33, 266.7) * mm});
            skLineSegment(sketch, "E170.top", {"start": v(64.64, 0) * mm, "end": v(59.33, 0) * mm});
            skArc(sketch, "E171", {"start": v(59.33, 266.7) * mm, "mid": v(44.42, 243.57) * mm, "end": v(59.33, 220.44) * mm});
            skArc(sketch, "E172", {"start": v(59.33, 220.44) * mm, "mid": v(43.94, 197.1) * mm, "end": v(59.33, 173.76) * mm});
            skArc(sketch, "E173", {"start": v(59.33, 173.76) * mm, "mid": v(45.63, 151.22) * mm, "end": v(59.33, 128.67) * mm});
            skArc(sketch, "E174", {"start": v(59.33, 128.67) * mm, "mid": v(43.92, 105.32) * mm, "end": v(59.33, 81.97) * mm});
            skArc(sketch, "E175", {"start": v(59.33, 81.97) * mm, "mid": v(43.09, 58.28) * mm, "end": v(59.33, 34.59) * mm});
            skArc(sketch, "E176", {"start": v(59.33, 34.59) * mm, "mid": v(42.03, 17.3) * mm, "end": v(59.33, 0) * mm});
            skLineSegment(sketch, "E177", {"start": v(59.33, 266.7) * mm, "end": v(72.87, 266.69) * mm});
            skLineSegment(sketch, "E178", {"start": v(59.33, 0) * mm, "end": v(72.87, -0.01) * mm});
            skLineSegment(sketch, "E179.bottom", {"start": v(52.37, 266.69) * mm, "end": v(47.06, 266.69) * mm});
            skLineSegment(sketch, "E179.top", {"start": v(52.37, -0.01) * mm, "end": v(47.06, -0.01) * mm});
            skArc(sketch, "E180", {"start": v(47.06, 266.69) * mm, "mid": v(32.15, 243.56) * mm, "end": v(47.06, 220.43) * mm});
            skArc(sketch, "E181", {"start": v(47.06, 220.43) * mm, "mid": v(31.67, 197.1) * mm, "end": v(47.06, 173.75) * mm});
            skArc(sketch, "E182", {"start": v(47.06, 173.75) * mm, "mid": v(33.36, 151.2) * mm, "end": v(47.06, 128.66) * mm});
            skArc(sketch, "E183", {"start": v(47.06, 128.66) * mm, "mid": v(31.65, 105.3) * mm, "end": v(47.06, 81.96) * mm});
            skArc(sketch, "E184", {"start": v(47.06, 81.96) * mm, "mid": v(30.82, 58.27) * mm, "end": v(47.06, 34.58) * mm});
            skArc(sketch, "E185", {"start": v(47.06, 34.58) * mm, "mid": v(29.76, 17.28) * mm, "end": v(47.06, -0.01) * mm});
            skLineSegment(sketch, "E186.bottom", {"start": v(38.83, 266.7) * mm, "end": v(33.51, 266.7) * mm});
            skLineSegment(sketch, "E186.top", {"start": v(38.83, 0) * mm, "end": v(33.51, 0) * mm});
            skArc(sketch, "E187", {"start": v(33.51, 266.7) * mm, "mid": v(18.6, 243.57) * mm, "end": v(33.51, 220.44) * mm});
            skArc(sketch, "E188", {"start": v(33.51, 220.44) * mm, "mid": v(18.13, 197.1) * mm, "end": v(33.51, 173.76) * mm});
            skArc(sketch, "E189", {"start": v(33.51, 173.76) * mm, "mid": v(19.81, 151.22) * mm, "end": v(33.51, 128.67) * mm});
            skArc(sketch, "E190", {"start": v(33.51, 128.67) * mm, "mid": v(18.1, 105.32) * mm, "end": v(33.51, 81.97) * mm});
            skArc(sketch, "E191", {"start": v(33.51, 81.97) * mm, "mid": v(17.27, 58.28) * mm, "end": v(33.51, 34.59) * mm});
            skArc(sketch, "E192", {"start": v(33.51, 34.59) * mm, "mid": v(16.22, 17.3) * mm, "end": v(33.51, 0) * mm});
            skLineSegment(sketch, "E193", {"start": v(33.51, 266.7) * mm, "end": v(47.06, 266.69) * mm});
            skLineSegment(sketch, "E194", {"start": v(33.51, 0) * mm, "end": v(47.06, -0.01) * mm});
            skLineSegment(sketch, "E195.bottom", {"start": v(27.31, 266.69) * mm, "end": v(22, 266.69) * mm});
            skLineSegment(sketch, "E195.top", {"start": v(27.31, -0.01) * mm, "end": v(22, -0.01) * mm});
            skArc(sketch, "E196", {"start": v(22, 266.69) * mm, "mid": v(7.1, 243.56) * mm, "end": v(22, 220.43) * mm});
            skArc(sketch, "E197", {"start": v(22, 220.43) * mm, "mid": v(6.61, 197.1) * mm, "end": v(22, 173.75) * mm});
            skArc(sketch, "E198", {"start": v(22, 173.75) * mm, "mid": v(8.3, 151.2) * mm, "end": v(22, 128.66) * mm});
            skArc(sketch, "E199", {"start": v(22, 128.66) * mm, "mid": v(6.58, 105.3) * mm, "end": v(22, 81.96) * mm});
            skArc(sketch, "E200", {"start": v(22, 81.96) * mm, "mid": v(5.75, 58.27) * mm, "end": v(22, 34.58) * mm});
            skArc(sketch, "E201", {"start": v(22, 34.58) * mm, "mid": v(4.7, 17.28) * mm, "end": v(22, -0.01) * mm});
            skLineSegment(sketch, "E202.bottom", {"start": v(13.77, 266.7) * mm, "end": v(8.45, 266.7) * mm});
            skLineSegment(sketch, "E202.top", {"start": v(13.77, 0) * mm, "end": v(8.45, 0) * mm});
            skArc(sketch, "E203", {"start": v(8.45, 266.7) * mm, "mid": v(-6.45, 243.57) * mm, "end": v(8.45, 220.44) * mm});
            skArc(sketch, "E204", {"start": v(8.45, 220.44) * mm, "mid": v(-6.93, 197.1) * mm, "end": v(8.45, 173.76) * mm});
            skArc(sketch, "E205", {"start": v(8.45, 173.76) * mm, "mid": v(-5.25, 151.22) * mm, "end": v(8.45, 128.67) * mm});
            skArc(sketch, "E206", {"start": v(8.45, 128.67) * mm, "mid": v(-6.96, 105.32) * mm, "end": v(8.45, 81.97) * mm});
            skArc(sketch, "E207", {"start": v(8.45, 81.97) * mm, "mid": v(-7.79, 58.28) * mm, "end": v(8.45, 34.59) * mm});
            skArc(sketch, "E208", {"start": v(8.45, 34.59) * mm, "mid": v(-8.84, 17.3) * mm, "end": v(8.45, 0) * mm});
            skLineSegment(sketch, "E209", {"start": v(8.45, 266.7) * mm, "end": v(22, 266.69) * mm});
            skLineSegment(sketch, "E210", {"start": v(8.45, 0) * mm, "end": v(22, -0.01) * mm});
            skLineSegment(sketch, "E211.bottom", {"start": v(6.05, 266.69) * mm, "end": v(0.73, 266.69) * mm});
            skLineSegment(sketch, "E211.top", {"start": v(6.05, -0.01) * mm, "end": v(0.73, -0.01) * mm});
            skArc(sketch, "E212", {"start": v(0.73, 266.69) * mm, "mid": v(-14.17, 243.56) * mm, "end": v(0.73, 220.43) * mm});
            skArc(sketch, "E213", {"start": v(0.73, 220.43) * mm, "mid": v(-14.65, 197.1) * mm, "end": v(0.73, 173.75) * mm});
            skArc(sketch, "E214", {"start": v(0.73, 173.75) * mm, "mid": v(-12.97, 151.2) * mm, "end": v(0.73, 128.66) * mm});
            skArc(sketch, "E215", {"start": v(0.73, 128.66) * mm, "mid": v(-14.68, 105.3) * mm, "end": v(0.73, 81.96) * mm});
            skArc(sketch, "E216", {"start": v(0.73, 81.96) * mm, "mid": v(-15.5, 58.27) * mm, "end": v(0.73, 34.58) * mm});
            skArc(sketch, "E217", {"start": v(0.73, 34.58) * mm, "mid": v(-16.56, 17.28) * mm, "end": v(0.73, -0.01) * mm});
            skLineSegment(sketch, "E218.bottom", {"start": v(-7.5, 266.7) * mm, "end": v(-12.81, 266.7) * mm});
            skLineSegment(sketch, "E218.top", {"start": v(-7.5, 0) * mm, "end": v(-12.81, 0) * mm});
            skArc(sketch, "E219", {"start": v(-12.81, 266.7) * mm, "mid": v(-27.71, 243.57) * mm, "end": v(-12.81, 220.44) * mm});
            skArc(sketch, "E220", {"start": v(-12.81, 220.44) * mm, "mid": v(-28.2, 197.1) * mm, "end": v(-12.81, 173.76) * mm});
            skArc(sketch, "E221", {"start": v(-12.81, 173.76) * mm, "mid": v(-26.5, 151.22) * mm, "end": v(-12.81, 128.67) * mm});
            skArc(sketch, "E222", {"start": v(-12.81, 128.67) * mm, "mid": v(-28.22, 105.32) * mm, "end": v(-12.81, 81.97) * mm});
            skArc(sketch, "E223", {"start": v(-12.81, 81.97) * mm, "mid": v(-29.05, 58.28) * mm, "end": v(-12.81, 34.59) * mm});
            skArc(sketch, "E224", {"start": v(-12.81, 34.59) * mm, "mid": v(-30.1, 17.3) * mm, "end": v(-12.81, 0) * mm});
            skLineSegment(sketch, "E225", {"start": v(-12.81, 266.7) * mm, "end": v(0.73, 266.69) * mm});
            skLineSegment(sketch, "E226", {"start": v(-12.81, 0) * mm, "end": v(0.73, -0.01) * mm});
            skSolve(sketch);
        }
        {
            var Q0;
            Q0 = qSketchRegion(id + "F24", true);
            extrude(context, id + "F25", {"entities" : qUnion([Q0]), "operationType" : NewBodyOperationType.ADD, "depth" : 5.08 * mm, "offsetDistance" : 25.4 * mm});
        }
        {
            var Q0;
            Q0=makeQuery(id+"F7.opExtrude","SWEPT_FACE",FACE,{"disambiguationData":[OSD([sQuery(id+"F6.wireOp",EDGE,"E27.0")])]});
            var sketch = newSketch(context, id + "F26", { "sketchPlane" : qUnion([Q0])});
            skLineSegment(sketch, "E227.bottom", {"start": v(-112, 0) * mm, "end": v(-106.68, 0) * mm});
            skLineSegment(sketch, "E227.top", {"start": v(-112, 266.7) * mm, "end": v(-106.68, 266.7) * mm});
            skLineSegment(sketch, "E227.left", {"start": v(-112, 0) * mm, "end": v(-112, 266.7) * mm});
            skLineSegment(sketch, "E228", {"start": v(-106.68, 0) * mm, "end": v(-106.68, 266.7) * mm});
            skLineSegment(sketch, "E229.bottom", {"start": v(-106.1, 0) * mm, "end": v(-100.79, 0) * mm});
            skLineSegment(sketch, "E229.top", {"start": v(-106.1, 266.7) * mm, "end": v(-100.79, 266.7) * mm});
            skArc(sketch, "E230", {"start": v(-100.79, 0) * mm, "mid": v(-85.89, 23.13) * mm, "end": v(-100.79, 46.26) * mm});
            skArc(sketch, "E231", {"start": v(-100.79, 46.26) * mm, "mid": v(-85.4, 69.6) * mm, "end": v(-100.79, 92.94) * mm});
            skArc(sketch, "E232", {"start": v(-100.79, 92.94) * mm, "mid": v(-87.1, 115.48) * mm, "end": v(-100.79, 138.03) * mm});
            skArc(sketch, "E233", {"start": v(-100.79, 138.03) * mm, "mid": v(-85.38, 161.38) * mm, "end": v(-100.79, 184.73) * mm});
            skArc(sketch, "E234", {"start": v(-100.79, 184.73) * mm, "mid": v(-84.55, 208.42) * mm, "end": v(-100.79, 232.11) * mm});
            skArc(sketch, "E235", {"start": v(-100.79, 232.11) * mm, "mid": v(-83.5, 249.4) * mm, "end": v(-100.79, 266.7) * mm});
            skLineSegment(sketch, "E236.bottom", {"start": v(-92.56, -0.01) * mm, "end": v(-87.24, -0.01) * mm});
            skLineSegment(sketch, "E236.top", {"start": v(-92.56, 266.69) * mm, "end": v(-87.24, 266.69) * mm});
            skArc(sketch, "E237", {"start": v(-87.24, -0.01) * mm, "mid": v(-72.34, 23.12) * mm, "end": v(-87.24, 46.25) * mm});
            skArc(sketch, "E238", {"start": v(-87.24, 46.25) * mm, "mid": v(-71.86, 69.59) * mm, "end": v(-87.24, 92.93) * mm});
            skArc(sketch, "E239", {"start": v(-87.24, 92.93) * mm, "mid": v(-73.55, 115.47) * mm, "end": v(-87.24, 138.02) * mm});
            skArc(sketch, "E240", {"start": v(-87.24, 138.02) * mm, "mid": v(-71.83, 161.37) * mm, "end": v(-87.24, 184.72) * mm});
            skArc(sketch, "E241", {"start": v(-87.24, 184.72) * mm, "mid": v(-71, 208.41) * mm, "end": v(-87.24, 232.1) * mm});
            skArc(sketch, "E242", {"start": v(-87.24, 232.1) * mm, "mid": v(-69.95, 249.4) * mm, "end": v(-87.24, 266.69) * mm});
            skLineSegment(sketch, "E243", {"start": v(-87.24, -0.01) * mm, "end": v(-100.79, 0) * mm});
            skLineSegment(sketch, "E244", {"start": v(-87.24, 266.69) * mm, "end": v(-100.79, 266.7) * mm});
            skLineSegment(sketch, "E245.bottom", {"start": v(-78.53, 0.01) * mm, "end": v(-73.21, 0.01) * mm});
            skLineSegment(sketch, "E245.top", {"start": v(-78.53, 266.71) * mm, "end": v(-73.21, 266.71) * mm});
            skArc(sketch, "E246", {"start": v(-73.21, 0.01) * mm, "mid": v(-58.3, 23.14) * mm, "end": v(-73.21, 46.27) * mm});
            skArc(sketch, "E247", {"start": v(-73.21, 46.27) * mm, "mid": v(-57.83, 69.6) * mm, "end": v(-73.21, 92.95) * mm});
            skArc(sketch, "E248", {"start": v(-73.21, 92.95) * mm, "mid": v(-59.51, 115.5) * mm, "end": v(-73.21, 138.04) * mm});
            skArc(sketch, "E249", {"start": v(-73.21, 138.04) * mm, "mid": v(-57.8, 161.4) * mm, "end": v(-73.21, 184.74) * mm});
            skArc(sketch, "E250", {"start": v(-73.21, 184.74) * mm, "mid": v(-56.97, 208.43) * mm, "end": v(-73.21, 232.12) * mm});
            skArc(sketch, "E251", {"start": v(-73.21, 232.12) * mm, "mid": v(-55.92, 249.42) * mm, "end": v(-73.21, 266.71) * mm});
            skLineSegment(sketch, "E252.bottom", {"start": v(-64.98, 0) * mm, "end": v(-59.67, 0) * mm});
            skLineSegment(sketch, "E252.top", {"start": v(-64.98, 266.7) * mm, "end": v(-59.67, 266.7) * mm});
            skArc(sketch, "E253", {"start": v(-59.67, 0) * mm, "mid": v(-44.76, 23.13) * mm, "end": v(-59.67, 46.26) * mm});
            skArc(sketch, "E254", {"start": v(-59.67, 46.26) * mm, "mid": v(-44.28, 69.6) * mm, "end": v(-59.67, 92.94) * mm});
            skArc(sketch, "E255", {"start": v(-59.67, 92.94) * mm, "mid": v(-45.97, 115.48) * mm, "end": v(-59.67, 138.03) * mm});
            skArc(sketch, "E256", {"start": v(-59.67, 138.03) * mm, "mid": v(-44.26, 161.38) * mm, "end": v(-59.67, 184.73) * mm});
            skArc(sketch, "E257", {"start": v(-59.67, 184.73) * mm, "mid": v(-43.43, 208.42) * mm, "end": v(-59.67, 232.11) * mm});
            skArc(sketch, "E258", {"start": v(-59.67, 232.11) * mm, "mid": v(-42.37, 249.4) * mm, "end": v(-59.67, 266.7) * mm});
            skLineSegment(sketch, "E259", {"start": v(-59.67, 0) * mm, "end": v(-73.21, 0.01) * mm});
            skLineSegment(sketch, "E260", {"start": v(-59.67, 266.7) * mm, "end": v(-73.21, 266.71) * mm});
            skLineSegment(sketch, "E261.bottom", {"start": v(-52.71, 0.01) * mm, "end": v(-47.4, 0.01) * mm});
            skLineSegment(sketch, "E261.top", {"start": v(-52.71, 266.71) * mm, "end": v(-47.4, 266.71) * mm});
            skArc(sketch, "E262", {"start": v(-47.4, 0.01) * mm, "mid": v(-32.5, 23.14) * mm, "end": v(-47.4, 46.27) * mm});
            skArc(sketch, "E263", {"start": v(-47.4, 46.27) * mm, "mid": v(-32.01, 69.6) * mm, "end": v(-47.4, 92.95) * mm});
            skArc(sketch, "E264", {"start": v(-47.4, 92.95) * mm, "mid": v(-33.7, 115.5) * mm, "end": v(-47.4, 138.04) * mm});
            skArc(sketch, "E265", {"start": v(-47.4, 138.04) * mm, "mid": v(-31.99, 161.4) * mm, "end": v(-47.4, 184.74) * mm});
            skArc(sketch, "E266", {"start": v(-47.4, 184.74) * mm, "mid": v(-31.16, 208.43) * mm, "end": v(-47.4, 232.12) * mm});
            skArc(sketch, "E267", {"start": v(-47.4, 232.12) * mm, "mid": v(-30.1, 249.42) * mm, "end": v(-47.4, 266.71) * mm});
            skLineSegment(sketch, "E268.bottom", {"start": v(-39.17, 0) * mm, "end": v(-33.85, 0) * mm});
            skLineSegment(sketch, "E268.top", {"start": v(-39.17, 266.7) * mm, "end": v(-33.85, 266.7) * mm});
            skArc(sketch, "E269", {"start": v(-33.85, 0) * mm, "mid": v(-18.95, 23.13) * mm, "end": v(-33.85, 46.26) * mm});
            skArc(sketch, "E270", {"start": v(-33.85, 46.26) * mm, "mid": v(-18.47, 69.6) * mm, "end": v(-33.85, 92.94) * mm});
            skArc(sketch, "E271", {"start": v(-33.85, 92.94) * mm, "mid": v(-20.15, 115.48) * mm, "end": v(-33.85, 138.03) * mm});
            skArc(sketch, "E272", {"start": v(-33.85, 138.03) * mm, "mid": v(-18.44, 161.38) * mm, "end": v(-33.85, 184.73) * mm});
            skArc(sketch, "E273", {"start": v(-33.85, 184.73) * mm, "mid": v(-17.61, 208.42) * mm, "end": v(-33.85, 232.11) * mm});
            skArc(sketch, "E274", {"start": v(-33.85, 232.11) * mm, "mid": v(-16.56, 249.4) * mm, "end": v(-33.85, 266.7) * mm});
            skLineSegment(sketch, "E275", {"start": v(-33.85, 0) * mm, "end": v(-47.4, 0.01) * mm});
            skLineSegment(sketch, "E276", {"start": v(-33.85, 266.7) * mm, "end": v(-47.4, 266.71) * mm});
            skLineSegment(sketch, "E277.bottom", {"start": v(-27.65, 0.01) * mm, "end": v(-22.33, 0.01) * mm});
            skLineSegment(sketch, "E277.top", {"start": v(-27.65, 266.71) * mm, "end": v(-22.33, 266.71) * mm});
            skArc(sketch, "E278", {"start": v(-22.33, 0.01) * mm, "mid": v(-7.43, 23.14) * mm, "end": v(-22.33, 46.27) * mm});
            skArc(sketch, "E279", {"start": v(-22.33, 46.27) * mm, "mid": v(-6.95, 69.6) * mm, "end": v(-22.33, 92.95) * mm});
            skArc(sketch, "E280", {"start": v(-22.33, 92.95) * mm, "mid": v(-8.64, 115.5) * mm, "end": v(-22.33, 138.04) * mm});
            skArc(sketch, "E281", {"start": v(-22.33, 138.04) * mm, "mid": v(-6.92, 161.4) * mm, "end": v(-22.33, 184.74) * mm});
            skArc(sketch, "E282", {"start": v(-22.33, 184.74) * mm, "mid": v(-6.1, 208.43) * mm, "end": v(-22.33, 232.12) * mm});
            skArc(sketch, "E283", {"start": v(-22.33, 232.12) * mm, "mid": v(-5.04, 249.42) * mm, "end": v(-22.33, 266.71) * mm});
            skLineSegment(sketch, "E284.bottom", {"start": v(-14.1, 0) * mm, "end": v(-8.79, 0) * mm});
            skLineSegment(sketch, "E284.top", {"start": v(-14.1, 266.7) * mm, "end": v(-8.79, 266.7) * mm});
            skArc(sketch, "E285", {"start": v(-8.79, 0) * mm, "mid": v(6.11, 23.13) * mm, "end": v(-8.79, 46.26) * mm});
            skArc(sketch, "E286", {"start": v(-8.79, 46.26) * mm, "mid": v(6.6, 69.6) * mm, "end": v(-8.79, 92.94) * mm});
            skArc(sketch, "E287", {"start": v(-8.79, 92.94) * mm, "mid": v(4.9, 115.48) * mm, "end": v(-8.79, 138.03) * mm});
            skArc(sketch, "E288", {"start": v(-8.79, 138.03) * mm, "mid": v(6.62, 161.38) * mm, "end": v(-8.79, 184.73) * mm});
            skArc(sketch, "E289", {"start": v(-8.79, 184.73) * mm, "mid": v(7.45, 208.42) * mm, "end": v(-8.79, 232.11) * mm});
            skArc(sketch, "E290", {"start": v(-8.79, 232.11) * mm, "mid": v(8.5, 249.4) * mm, "end": v(-8.79, 266.7) * mm});
            skLineSegment(sketch, "E291", {"start": v(-8.79, 0) * mm, "end": v(-22.33, 0.01) * mm});
            skLineSegment(sketch, "E292", {"start": v(-8.79, 266.7) * mm, "end": v(-22.33, 266.71) * mm});
            skLineSegment(sketch, "E293.bottom", {"start": v(-6.4, 0.01) * mm, "end": v(-1.07, 0.01) * mm});
            skLineSegment(sketch, "E293.top", {"start": v(-6.4, 266.71) * mm, "end": v(-1.07, 266.71) * mm});
            skArc(sketch, "E294", {"start": v(-1.07, 0.01) * mm, "mid": v(13.83, 23.14) * mm, "end": v(-1.07, 46.27) * mm});
            skArc(sketch, "E295", {"start": v(-1.07, 46.27) * mm, "mid": v(14.31, 69.6) * mm, "end": v(-1.07, 92.95) * mm});
            skArc(sketch, "E296", {"start": v(-1.07, 92.95) * mm, "mid": v(12.62, 115.5) * mm, "end": v(-1.07, 138.04) * mm});
            skArc(sketch, "E297", {"start": v(-1.07, 138.04) * mm, "mid": v(14.34, 161.4) * mm, "end": v(-1.07, 184.74) * mm});
            skArc(sketch, "E298", {"start": v(-1.07, 184.74) * mm, "mid": v(15.17, 208.43) * mm, "end": v(-1.07, 232.12) * mm});
            skArc(sketch, "E299", {"start": v(-1.07, 232.12) * mm, "mid": v(16.22, 249.42) * mm, "end": v(-1.07, 266.71) * mm});
            skLineSegment(sketch, "E300.bottom", {"start": v(7.15, 0) * mm, "end": v(12.47, 0) * mm});
            skLineSegment(sketch, "E300.top", {"start": v(7.15, 266.7) * mm, "end": v(12.47, 266.7) * mm});
            skArc(sketch, "E301", {"start": v(12.47, 0) * mm, "mid": v(27.37, 23.13) * mm, "end": v(12.47, 46.26) * mm});
            skArc(sketch, "E302", {"start": v(12.47, 46.26) * mm, "mid": v(27.86, 69.6) * mm, "end": v(12.47, 92.94) * mm});
            skArc(sketch, "E303", {"start": v(12.47, 92.94) * mm, "mid": v(26.17, 115.48) * mm, "end": v(12.47, 138.03) * mm});
            skArc(sketch, "E304", {"start": v(12.47, 138.03) * mm, "mid": v(27.88, 161.38) * mm, "end": v(12.47, 184.73) * mm});
            skArc(sketch, "E305", {"start": v(12.47, 184.73) * mm, "mid": v(28.71, 208.42) * mm, "end": v(12.47, 232.11) * mm});
            skArc(sketch, "E306", {"start": v(12.47, 232.11) * mm, "mid": v(29.77, 249.4) * mm, "end": v(12.47, 266.7) * mm});
            skLineSegment(sketch, "E307", {"start": v(12.47, 0) * mm, "end": v(-1.07, 0.01) * mm});
            skLineSegment(sketch, "E308", {"start": v(12.47, 266.7) * mm, "end": v(-1.07, 266.71) * mm});
            skSolve(sketch);
        }
        {
            var Q0;
            Q0 = qSketchRegion(id + "F26", true);
            extrude(context, id + "F27", {"entities" : qUnion([Q0]), "operationType" : NewBodyOperationType.ADD, "depth" : 5.08 * mm, "offsetDistance" : 25.4 * mm});
        }
        {
            var Q0;
            Q0=makeQuery(id+"F3.opExtrude","SWEPT_FACE",FACE,{"disambiguationData":[OSD([sQuery(id+"F2.wireOp",EDGE,"E7")])]});
            var sketch = newSketch(context, id + "F28", { "sketchPlane" : qUnion([Q0])});
            skLineSegment(sketch, "E309.bottom", {"start": v(-26.02, 101.6) * mm, "end": v(24.78, 101.6) * mm});
            skLineSegment(sketch, "E309.left", {"start": v(-26.02, 101.6) * mm, "end": v(-26.02, 4.24) * mm});
            skLineSegment(sketch, "E309.right", {"start": v(24.78, 101.6) * mm, "end": v(24.78, 4.24) * mm});
            skLineSegment(sketch, "E310", {"start": v(-30.07, 0) * mm, "end": v(-30.07, 105.53) * mm});
            skLineSegment(sketch, "E311", {"start": v(-30.07, 105.53) * mm, "end": v(28.83, 105.53) * mm});
            skLineSegment(sketch, "E312", {"start": v(28.83, 105.53) * mm, "end": v(28.83, 0) * mm});
            skLineSegment(sketch, "E313", {"start": v(-26.02, 4.24) * mm, "end": v(24.78, 4.24) * mm});
            skPoint(sketch, "E314.start.orphan", {"position": v(-26.02, 0) * mm});
            skLineSegment(sketch, "E315", {"start": v(-30.07, 0) * mm, "end": v(28.83, 0) * mm});
            skSolve(sketch);
        }
        {
            var Q0;
            Q0 = qSketchRegion(id + "F28", true);
            extrude(context, id + "F29", {"entities" : qUnion([Q0]), "operationType" : NewBodyOperationType.ADD, "depth" : 5.08 * mm, "offsetDistance" : 25.4 * mm});
        }
        {
            var Q0;
            Q0=makeQuery(id+"F29.boolean.opBoolean","SPLIT",FACE,{"disambiguationData":[TD([makeQuery(id+"F29.opExtrude","SWEPT_FACE",FACE,{"disambiguationData":[OSD([sQuery(id+"F28.wireOp",EDGE,"E309.bottom")])]})])],"derivedFrom":makeQuery(id+"F3.opExtrude","SWEPT_FACE",FACE,{"disambiguationData":[OSD([sQuery(id+"F2.wireOp",EDGE,"E7")])]})});
            var sketch = newSketch(context, id + "F30", { "sketchPlane" : qUnion([Q0])});
            skArc(sketch, "E316", {"start": v(14.7, 77.28) * mm, "mid": v(-1.26, 93.13) * mm, "end": v(-17.22, 77.28) * mm});
            skArc(sketch, "E317", {"start": v(18.55, 73.76) * mm, "mid": v(-0.83, 96.78) * mm, "end": v(-20.2, 73.76) * mm});
            skLineSegment(sketch, "E318", {"start": v(14.7, 77.28) * mm, "end": v(-17.22, 77.28) * mm});
            skLineSegment(sketch, "E319", {"start": v(-20.2, 73.76) * mm, "end": v(18.55, 73.76) * mm});
            skLineSegment(sketch, "E320.bottom", {"start": v(-1.26, 93.13) * mm, "end": v(1.33, 93.13) * mm});
            skLineSegment(sketch, "E320.top", {"start": v(-1.26, 77.28) * mm, "end": v(1.33, 77.28) * mm});
            skLineSegment(sketch, "E321.bottom", {"start": v(5.52, 62.94) * mm, "end": v(14.28, 62.94) * mm});
            skLineSegment(sketch, "E321.top", {"start": v(5.52, 43.51) * mm, "end": v(14.28, 43.51) * mm});
            skLineSegment(sketch, "E321.left", {"start": v(5.52, 62.94) * mm, "end": v(5.52, 43.51) * mm});
            skLineSegment(sketch, "E321.right", {"start": v(14.28, 62.94) * mm, "end": v(14.28, 43.51) * mm});
            skLineSegment(sketch, "E322.bottom", {"start": v(16.74, 65.4) * mm, "end": v(3.06, 65.4) * mm});
            skLineSegment(sketch, "E322.top", {"start": v(16.74, 40.78) * mm, "end": v(3.06, 40.78) * mm});
            skLineSegment(sketch, "E322.left", {"start": v(16.74, 65.4) * mm, "end": v(16.74, 40.78) * mm});
            skLineSegment(sketch, "E322.right", {"start": v(3.06, 65.4) * mm, "end": v(3.06, 40.78) * mm});
            skLineSegment(sketch, "E323.bottom", {"start": v(-15.27, 62.94) * mm, "end": v(-6.52, 62.94) * mm});
            skLineSegment(sketch, "E323.top", {"start": v(-15.27, 43.51) * mm, "end": v(-6.52, 43.51) * mm});
            skLineSegment(sketch, "E323.left", {"start": v(-15.27, 62.94) * mm, "end": v(-15.27, 43.51) * mm});
            skLineSegment(sketch, "E323.right", {"start": v(-6.52, 62.94) * mm, "end": v(-6.52, 43.51) * mm});
            skLineSegment(sketch, "E324.bottom", {"start": v(-4.05, 65.4) * mm, "end": v(-17.74, 65.4) * mm});
            skLineSegment(sketch, "E324.top", {"start": v(-4.05, 40.78) * mm, "end": v(-17.74, 40.78) * mm});
            skLineSegment(sketch, "E324.left", {"start": v(-4.05, 65.4) * mm, "end": v(-4.05, 40.78) * mm});
            skLineSegment(sketch, "E324.right", {"start": v(-17.74, 65.4) * mm, "end": v(-17.74, 40.78) * mm});
            skLineSegment(sketch, "E325.bottom", {"start": v(5.52, 33.05) * mm, "end": v(14.28, 33.05) * mm});
            skLineSegment(sketch, "E325.top", {"start": v(5.52, 13.62) * mm, "end": v(14.28, 13.62) * mm});
            skLineSegment(sketch, "E325.left", {"start": v(5.52, 33.05) * mm, "end": v(5.52, 13.62) * mm});
            skLineSegment(sketch, "E325.right", {"start": v(14.28, 33.05) * mm, "end": v(14.28, 13.62) * mm});
            skLineSegment(sketch, "E326.bottom", {"start": v(16.74, 35.5) * mm, "end": v(3.06, 35.5) * mm});
            skLineSegment(sketch, "E326.top", {"start": v(16.74, 10.88) * mm, "end": v(3.06, 10.88) * mm});
            skLineSegment(sketch, "E326.left", {"start": v(16.74, 35.5) * mm, "end": v(16.74, 10.88) * mm});
            skLineSegment(sketch, "E326.right", {"start": v(3.06, 35.5) * mm, "end": v(3.06, 10.88) * mm});
            skLineSegment(sketch, "E327.bottom", {"start": v(-14.73, 33.05) * mm, "end": v(-5.97, 33.05) * mm});
            skLineSegment(sketch, "E327.top", {"start": v(-14.73, 13.62) * mm, "end": v(-5.97, 13.62) * mm});
            skLineSegment(sketch, "E327.left", {"start": v(-14.73, 33.05) * mm, "end": v(-14.73, 13.62) * mm});
            skLineSegment(sketch, "E327.right", {"start": v(-5.97, 33.05) * mm, "end": v(-5.97, 13.62) * mm});
            skLineSegment(sketch, "E328.bottom", {"start": v(-3.5, 35.5) * mm, "end": v(-17.19, 35.5) * mm});
            skLineSegment(sketch, "E328.top", {"start": v(-3.5, 10.88) * mm, "end": v(-17.19, 10.88) * mm});
            skLineSegment(sketch, "E328.left", {"start": v(-3.5, 35.5) * mm, "end": v(-3.5, 10.88) * mm});
            skLineSegment(sketch, "E328.right", {"start": v(-17.19, 35.5) * mm, "end": v(-17.19, 10.88) * mm});
            skCircle(sketch, "E329", {"center": v(20.79, 47.34) * mm, "radius": 1.36 * mm});
            skCircle(sketch, "E330", {"center": v(20.79, 47.34) * mm, "radius": 2.25 * mm});
            skLineSegment(sketch, "E331", {"start": v(-13.84, 87) * mm, "end": v(-7.14, 77.28) * mm});
            skLineSegment(sketch, "E332", {"start": v(-7.14, 77.28) * mm, "end": v(-5.32, 77.28) * mm});
            skLineSegment(sketch, "E333", {"start": v(-5.32, 77.28) * mm, "end": v(-12.72, 88.28) * mm});
            skLineSegment(sketch, "E334", {"start": v(-12.72, 88.28) * mm, "end": v(-13.84, 87) * mm});
            skLineSegment(sketch, "E335.bottom", {"start": v(-69.12, 153.86) * mm, "end": v(-61.93, 153.86) * mm});
            skLineSegment(sketch, "E335.top", {"start": v(-69.12, 121.47) * mm, "end": v(-61.93, 121.47) * mm});
            skLineSegment(sketch, "E335.left", {"start": v(-69.12, 153.86) * mm, "end": v(-69.12, 121.47) * mm});
            skLineSegment(sketch, "E335.right", {"start": v(-61.93, 153.86) * mm, "end": v(-61.93, 121.47) * mm});
            skLineSegment(sketch, "E336.bottom", {"start": v(-69.12, 117.03) * mm, "end": v(-61.93, 117.03) * mm});
            skLineSegment(sketch, "E336.top", {"start": v(-69.12, 84.63) * mm, "end": v(-61.93, 84.63) * mm});
            skLineSegment(sketch, "E336.left", {"start": v(-69.12, 117.03) * mm, "end": v(-69.12, 84.63) * mm});
            skLineSegment(sketch, "E336.right", {"start": v(-61.93, 117.03) * mm, "end": v(-61.93, 84.63) * mm});
            skLineSegment(sketch, "E337.bottom", {"start": v(-69.12, 81.37) * mm, "end": v(-61.93, 81.37) * mm});
            skLineSegment(sketch, "E337.top", {"start": v(-69.12, 48.98) * mm, "end": v(-61.93, 48.98) * mm});
            skLineSegment(sketch, "E337.left", {"start": v(-69.12, 81.37) * mm, "end": v(-69.12, 48.98) * mm});
            skLineSegment(sketch, "E337.right", {"start": v(-61.93, 81.37) * mm, "end": v(-61.93, 48.98) * mm});
            skLineSegment(sketch, "E338.bottom", {"start": v(-69.12, 46.05) * mm, "end": v(-61.93, 46.05) * mm});
            skLineSegment(sketch, "E338.top", {"start": v(-69.12, 13.65) * mm, "end": v(-61.93, 13.65) * mm});
            skLineSegment(sketch, "E338.left", {"start": v(-69.12, 46.05) * mm, "end": v(-69.12, 13.65) * mm});
            skLineSegment(sketch, "E338.right", {"start": v(-61.93, 46.05) * mm, "end": v(-61.93, 13.65) * mm});
            skLineSegment(sketch, "E339.bottom", {"start": v(-69.12, 10.12) * mm, "end": v(-61.93, 10.12) * mm});
            skLineSegment(sketch, "E339.top", {"start": v(-69.12, 0) * mm, "end": v(-61.93, 0) * mm});
            skLineSegment(sketch, "E339.left", {"start": v(-69.12, 10.12) * mm, "end": v(-69.12, 0) * mm});
            skLineSegment(sketch, "E339.right", {"start": v(-61.93, 10.12) * mm, "end": v(-61.93, 0) * mm});
            skLineSegment(sketch, "E340.bottom", {"start": v(61.62, 153.86) * mm, "end": v(68.81, 153.86) * mm});
            skLineSegment(sketch, "E340.top", {"start": v(61.62, 121.47) * mm, "end": v(68.81, 121.47) * mm});
            skLineSegment(sketch, "E340.left", {"start": v(61.62, 153.86) * mm, "end": v(61.62, 121.47) * mm});
            skLineSegment(sketch, "E340.right", {"start": v(68.81, 153.86) * mm, "end": v(68.81, 121.47) * mm});
            skLineSegment(sketch, "E341.bottom", {"start": v(61.62, 117.03) * mm, "end": v(68.81, 117.03) * mm});
            skLineSegment(sketch, "E341.top", {"start": v(61.62, 84.63) * mm, "end": v(68.81, 84.63) * mm});
            skLineSegment(sketch, "E341.left", {"start": v(61.62, 117.03) * mm, "end": v(61.62, 84.63) * mm});
            skLineSegment(sketch, "E341.right", {"start": v(68.81, 117.03) * mm, "end": v(68.81, 84.63) * mm});
            skLineSegment(sketch, "E342.bottom", {"start": v(61.62, 81.37) * mm, "end": v(68.81, 81.37) * mm});
            skLineSegment(sketch, "E342.top", {"start": v(61.62, 48.98) * mm, "end": v(68.81, 48.98) * mm});
            skLineSegment(sketch, "E342.left", {"start": v(61.62, 81.37) * mm, "end": v(61.62, 48.98) * mm});
            skLineSegment(sketch, "E342.right", {"start": v(68.81, 81.37) * mm, "end": v(68.81, 48.98) * mm});
            skLineSegment(sketch, "E343.bottom", {"start": v(61.62, 46.05) * mm, "end": v(68.81, 46.05) * mm});
            skLineSegment(sketch, "E343.top", {"start": v(61.62, 13.65) * mm, "end": v(68.81, 13.65) * mm});
            skLineSegment(sketch, "E343.left", {"start": v(61.62, 46.05) * mm, "end": v(61.62, 13.65) * mm});
            skLineSegment(sketch, "E343.right", {"start": v(68.81, 46.05) * mm, "end": v(68.81, 13.65) * mm});
            skLineSegment(sketch, "E344.bottom", {"start": v(61.62, 10.12) * mm, "end": v(68.81, 10.12) * mm});
            skLineSegment(sketch, "E344.top", {"start": v(61.62, 0) * mm, "end": v(68.81, 0) * mm});
            skLineSegment(sketch, "E344.left", {"start": v(61.62, 10.12) * mm, "end": v(61.62, 0) * mm});
            skLineSegment(sketch, "E344.right", {"start": v(68.81, 10.12) * mm, "end": v(68.81, 0) * mm});
            skSolve(sketch);
        }
        {
            var Q0;
            Q0 = qSketchRegion(id + "F30", true);
            extrude(context, id + "F31", {"entities" : qUnion([Q0]), "operationType" : NewBodyOperationType.ADD, "depth" : 5.08 * mm, "offsetDistance" : 25.4 * mm});
        }
        {
            var Q0;
            Q0=makeQuery(id+"F27.opExtrude","CAP_FACE",FACE,{"disambiguationData":[OSD([sQuery(id+"F26.wireOp",EDGE,"E246"),sQuery(id+"F26.wireOp",EDGE,"E247"),sQuery(id+"F26.wireOp",EDGE,"E248"),sQuery(id+"F26.wireOp",EDGE,"E249"),sQuery(id+"F26.wireOp",EDGE,"E250"),sQuery(id+"F26.wireOp",EDGE,"E251"),sQuery(id+"F26.wireOp",EDGE,"E253"),sQuery(id+"F26.wireOp",EDGE,"E254"),sQuery(id+"F26.wireOp",EDGE,"E255"),sQuery(id+"F26.wireOp",EDGE,"E256"),sQuery(id+"F26.wireOp",EDGE,"E257"),sQuery(id+"F26.wireOp",EDGE,"E258"),sQuery(id+"F26.wireOp",EDGE,"E259"),sQuery(id+"F26.wireOp",EDGE,"E260")])],"isStart":false});
            var sketch = newSketch(context, id + "F32", { "sketchPlane" : qUnion([Q0])});
            skLineSegment(sketch, "E345.bottom", {"start": v(-73.21, 173.35) * mm, "end": v(-35.35, 173.35) * mm});
            skLineSegment(sketch, "E345.top", {"start": v(-73.21, 222.08) * mm, "end": v(-35.35, 222.08) * mm});
            skLineSegment(sketch, "E345.left", {"start": v(-73.21, 173.35) * mm, "end": v(-73.21, 222.08) * mm});
            skLineSegment(sketch, "E345.right", {"start": v(-35.35, 173.35) * mm, "end": v(-35.35, 222.08) * mm});
            skSolve(sketch);
        }
        {
            var Q0;
            Q0 = qSketchRegion(id + "F32", true);
            extrude(context, id + "F33", {"entities" : qUnion([Q0]), "operationType" : NewBodyOperationType.ADD, "depth" : 37.85 * mm, "offsetDistance" : 25.4 * mm});
        }
        {
            var Q0;
            Q0=makeQuery(id+"F33.opExtrude","CAP_FACE",FACE,{"disambiguationData":[OSD([sQuery(id+"F32.wireOp",EDGE,"E345.bottom"),sQuery(id+"F32.wireOp",EDGE,"E345.top"),sQuery(id+"F32.wireOp",EDGE,"E345.left"),sQuery(id+"F32.wireOp",EDGE,"E345.right")])],"isStart":false});
            var sketch = newSketch(context, id + "F34", { "sketchPlane" : qUnion([Q0])});
            skLineSegment(sketch, "E346.bottom", {"start": v(-67.57, 180.55) * mm, "end": v(-42.77, 180.55) * mm});
            skLineSegment(sketch, "E346.top", {"start": v(-67.57, 216.13) * mm, "end": v(-42.77, 216.13) * mm});
            skLineSegment(sketch, "E346.left", {"start": v(-67.57, 180.55) * mm, "end": v(-67.57, 216.13) * mm});
            skLineSegment(sketch, "E346.right", {"start": v(-42.77, 180.55) * mm, "end": v(-42.77, 216.13) * mm});
            skLineSegment(sketch, "E347.bottom", {"start": v(-78.81, 168.87) * mm, "end": v(-31.25, 168.87) * mm});
            skLineSegment(sketch, "E347.top", {"start": v(-78.81, 226.9) * mm, "end": v(-31.25, 226.9) * mm});
            skLineSegment(sketch, "E347.left", {"start": v(-78.81, 168.87) * mm, "end": v(-78.81, 226.9) * mm});
            skLineSegment(sketch, "E347.right", {"start": v(-31.25, 168.87) * mm, "end": v(-31.25, 226.9) * mm});
            skSolve(sketch);
        }
        {
            var Q0;
            Q0 = qSketchRegion(id + "F34", true);
            extrude(context, id + "F35", {"entities" : qUnion([Q0]), "operationType" : NewBodyOperationType.ADD, "depth" : 12.7 * mm, "offsetDistance" : 25.4 * mm});
        }
    });
